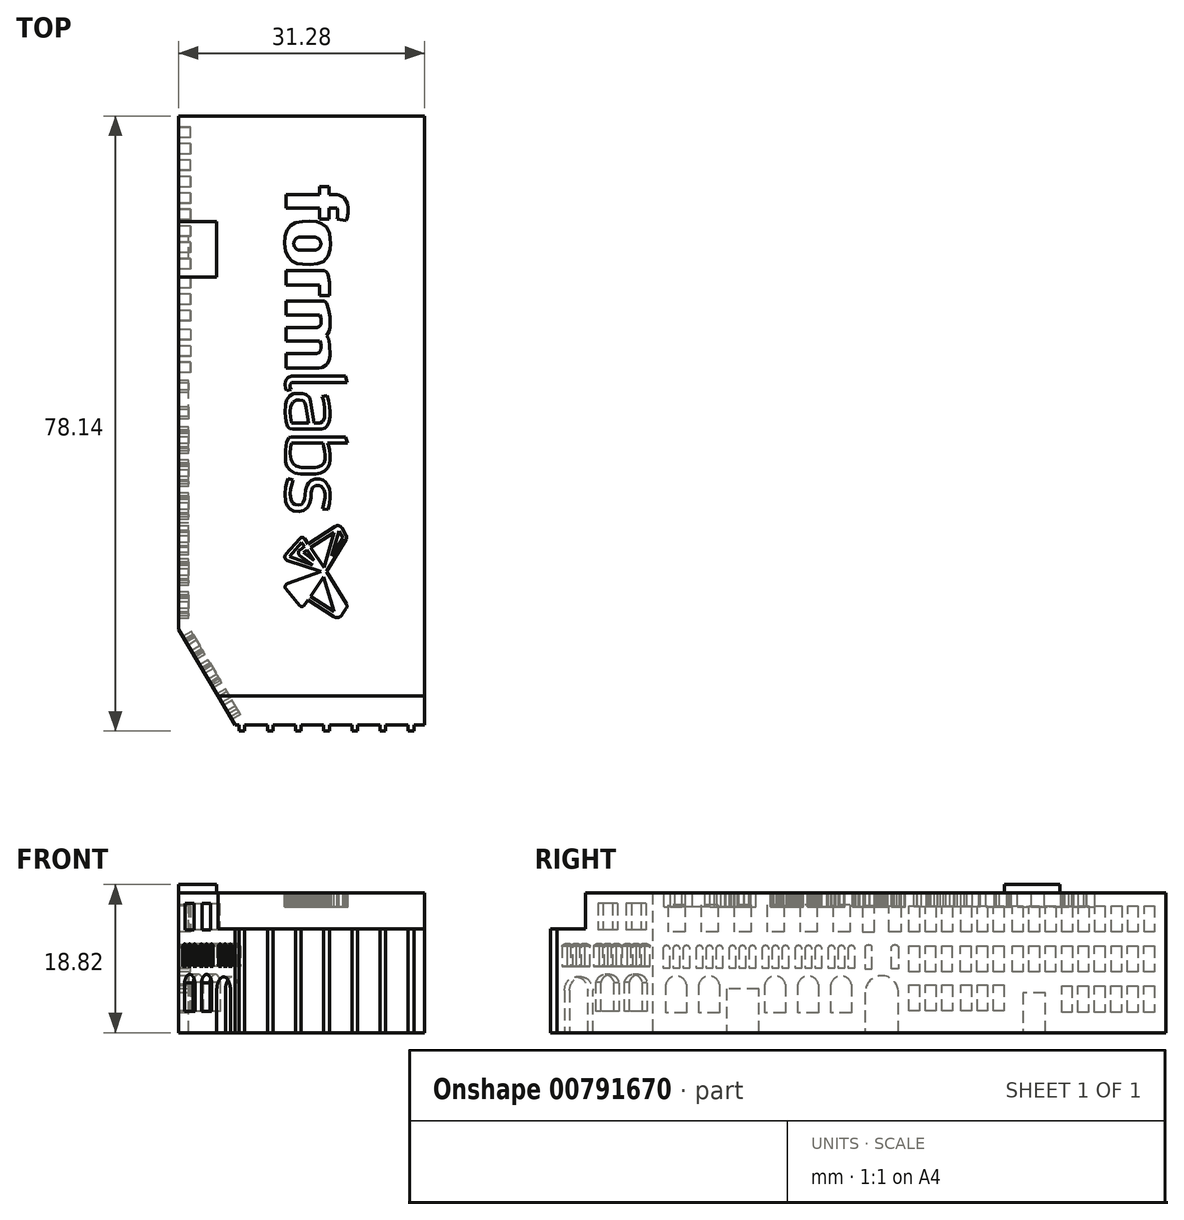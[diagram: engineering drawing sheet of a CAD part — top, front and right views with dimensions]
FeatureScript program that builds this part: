
annotation { "Feature Type Name" : "Feature", "Feature Type Description" : "" }
export const myFeature = defineFeature(function(context is Context, id is Id, definition is map)
    precondition{}
    {
        {
            var Q0;
            Q0=qCreatedBy(makeId("Top.planeOp"),FACE);
            var sketch = newSketch(context, id + "F0", { "sketchPlane" : qUnion([Q0])});
            skLineSegment(sketch, "E0", {"start": v(-16.51, -36.2) * mm, "end": v(-16.51, 29.03) * mm});
            skLineSegment(sketch, "E1", {"start": v(-16.51, 29.03) * mm, "end": v(14.77, 29.03) * mm});
            skLineSegment(sketch, "E2", {"start": v(14.77, 29.03) * mm, "end": v(14.77, -48.33) * mm});
            skLineSegment(sketch, "E3", {"start": v(14.77, -48.33) * mm, "end": v(-9.3, -48.33) * mm});
            skLineSegment(sketch, "E4", {"start": v(-9.3, -48.33) * mm, "end": v(-16.51, -36.2) * mm});
            skSolve(sketch);
        }
        {
            var Q0;
            Q0 = qSketchRegion(id + "F0", true);
            extrude(context, id + "F1", {"entities" : qUnion([Q0]), "depth" : 13.2 * mm, "offsetDistance" : 25.4 * mm});
        }
        {
            var Q0;
            Q0=makeQuery(id+"F1.opExtrude","CAP_FACE",FACE,{"disambiguationData":[OSD([sQuery(id+"F0.wireOp",EDGE,"E0"),sQuery(id+"F0.wireOp",EDGE,"E1"),sQuery(id+"F0.wireOp",EDGE,"E2"),sQuery(id+"F0.wireOp",EDGE,"E3"),sQuery(id+"F0.wireOp",EDGE,"E4")])],"isStart":false});
            var sketch = newSketch(context, id + "F2", { "sketchPlane" : qUnion([Q0])});
            skLineSegment(sketch, "E5", {"start": v(14.77, -44.68) * mm, "end": v(-11.47, -44.68) * mm});
            skLineSegment(sketch, "E6", {"start": v(-11.47, -44.68) * mm, "end": v(-16.51, -36.2) * mm});
            skLineSegment(sketch, "E7", {"start": v(-16.51, -36.2) * mm, "end": v(-16.51, 29.03) * mm});
            skLineSegment(sketch, "E8", {"start": v(-16.51, 29.03) * mm, "end": v(14.77, 29.03) * mm});
            skLineSegment(sketch, "E9", {"start": v(14.77, 29.03) * mm, "end": v(14.77, -44.68) * mm});
            skSolve(sketch);
        }
        {
            var Q0;
            Q0 = qSketchRegion(id + "F2", true);
            extrude(context, id + "F3", {"entities" : qUnion([Q0]), "operationType" : NewBodyOperationType.ADD, "depth" : 4.57 * mm, "offsetDistance" : 25.4 * mm});
        }
        {
            var Q0;
            Q0=makeQuery(id+"F3.opExtrude","CAP_FACE",FACE,{"disambiguationData":[OSD([sQuery(id+"F2.wireOp",EDGE,"E5"),sQuery(id+"F2.wireOp",EDGE,"E6"),sQuery(id+"F2.wireOp",EDGE,"E7"),sQuery(id+"F2.wireOp",EDGE,"E8"),sQuery(id+"F2.wireOp",EDGE,"E9")])],"isStart":false});
            var sketch = newSketch(context, id + "F4", { "sketchPlane" : qUnion([Q0])});
            skLineSegment(sketch, "E10", {"start": v(-16.51, 15.61) * mm, "end": v(-11.69, 15.61) * mm});
            skLineSegment(sketch, "E11", {"start": v(-11.69, 15.61) * mm, "end": v(-11.69, 8.53) * mm});
            skLineSegment(sketch, "E12", {"start": v(-11.69, 8.53) * mm, "end": v(-16.51, 8.53) * mm});
            skLineSegment(sketch, "E13", {"start": v(-16.51, 8.53) * mm, "end": v(-16.51, 15.61) * mm});
            skSolve(sketch);
        }
        {
            var Q0;
            Q0 = qSketchRegion(id + "F4", true);
            extrude(context, id + "F5", {"entities" : qUnion([Q0]), "operationType" : NewBodyOperationType.ADD, "depth" : 1.04 * mm, "offsetDistance" : 25.4 * mm});
        }
        {
            var Q0;
            Q0=makeQuery(id+"F5.boolean.opBoolean","MERGE",FACE,{"derivedFrom":[makeQuery(id+"F3.boolean.opBoolean","MERGE",FACE,{"derivedFrom":[makeQuery(id+"F1.opExtrude","SWEPT_FACE",FACE,{"disambiguationData":[OSD([sQuery(id+"F0.wireOp",EDGE,"E0")])]}),makeQuery(id+"F3.opExtrude","SWEPT_FACE",FACE,{"disambiguationData":[OSD([sQuery(id+"F2.wireOp",EDGE,"E7")])]})]}),makeQuery(id+"F5.opExtrude","SWEPT_FACE",FACE,{"disambiguationData":[OSD([sQuery(id+"F4.wireOp",EDGE,"E13")])]})]});
            var sketch = newSketch(context, id + "F6", { "sketchPlane" : qUnion([Q0])});
            skLineSegment(sketch, "E14", {"start": v(-27.6, 16.12) * mm, "end": v(-27.6, 12.8) * mm});
            skLineSegment(sketch, "E15", {"start": v(-27.6, 12.8) * mm, "end": v(-26.29, 12.8) * mm});
            skLineSegment(sketch, "E16", {"start": v(-26.29, 12.8) * mm, "end": v(-26.29, 16.12) * mm});
            skLineSegment(sketch, "E17", {"start": v(-26.29, 16.12) * mm, "end": v(-27.6, 16.12) * mm});
            skLineSegment(sketch, "E18.1.0.0", {"start": v(-25.52, 16.12) * mm, "end": v(-25.52, 12.8) * mm});
            skLineSegment(sketch, "E18.1.0.1", {"start": v(-25.52, 12.8) * mm, "end": v(-24.2, 12.8) * mm});
            skLineSegment(sketch, "E18.1.0.2", {"start": v(-24.2, 12.8) * mm, "end": v(-24.2, 16.12) * mm});
            skLineSegment(sketch, "E18.1.0.3", {"start": v(-24.2, 16.12) * mm, "end": v(-25.52, 16.12) * mm});
            skLineSegment(sketch, "E18.2.0.0", {"start": v(-23.44, 16.12) * mm, "end": v(-23.44, 12.8) * mm});
            skLineSegment(sketch, "E18.2.0.1", {"start": v(-23.44, 12.8) * mm, "end": v(-22.12, 12.8) * mm});
            skLineSegment(sketch, "E18.2.0.2", {"start": v(-22.12, 12.8) * mm, "end": v(-22.12, 16.12) * mm});
            skLineSegment(sketch, "E18.2.0.3", {"start": v(-22.12, 16.12) * mm, "end": v(-23.44, 16.12) * mm});
            skLineSegment(sketch, "E18.direction1", {"start": v(-27.6, 12.8) * mm, "end": v(-25.52, 12.8) * mm, "construction": true});
            skLineSegment(sketch, "E19.1.0.0", {"start": v(-24.19, 7.7) * mm, "end": v(-24.19, 11.02) * mm});
            skLineSegment(sketch, "E19.1.0.1", {"start": v(-24.19, 11.02) * mm, "end": v(-25.5, 11.02) * mm});
            skLineSegment(sketch, "E19.1.0.2", {"start": v(-27.58, 7.7) * mm, "end": v(-25.5, 7.7) * mm, "construction": true});
            skLineSegment(sketch, "E19.1.0.3", {"start": v(-22.1, 11.02) * mm, "end": v(-23.42, 11.02) * mm});
            skLineSegment(sketch, "E19.1.0.4", {"start": v(-25.5, 7.7) * mm, "end": v(-24.19, 7.7) * mm});
            skLineSegment(sketch, "E19.1.0.5", {"start": v(-23.42, 11.02) * mm, "end": v(-23.42, 7.7) * mm});
            skLineSegment(sketch, "E19.1.0.6", {"start": v(-22.1, 7.7) * mm, "end": v(-22.1, 11.02) * mm});
            skLineSegment(sketch, "E19.1.0.7", {"start": v(-25.5, 11.02) * mm, "end": v(-25.5, 7.7) * mm});
            skLineSegment(sketch, "E19.1.0.8", {"start": v(-23.42, 7.7) * mm, "end": v(-22.1, 7.7) * mm});
            skLineSegment(sketch, "E19.1.0.9", {"start": v(-26.27, 11.02) * mm, "end": v(-27.58, 11.02) * mm});
            skLineSegment(sketch, "E19.1.0.10", {"start": v(-27.58, 11.02) * mm, "end": v(-27.58, 7.7) * mm});
            skLineSegment(sketch, "E19.1.0.11", {"start": v(-26.27, 7.7) * mm, "end": v(-26.27, 11.02) * mm});
            skLineSegment(sketch, "E19.1.0.12", {"start": v(-27.58, 7.7) * mm, "end": v(-26.27, 7.7) * mm});
            skLineSegment(sketch, "E19.2.0.0", {"start": v(-24.17, 2.6) * mm, "end": v(-24.17, 5.92) * mm});
            skLineSegment(sketch, "E19.2.0.1", {"start": v(-24.17, 5.92) * mm, "end": v(-25.48, 5.92) * mm});
            skLineSegment(sketch, "E19.2.0.2", {"start": v(-27.57, 2.6) * mm, "end": v(-25.48, 2.6) * mm, "construction": true});
            skLineSegment(sketch, "E19.2.0.3", {"start": v(-22.08, 5.92) * mm, "end": v(-23.4, 5.92) * mm});
            skLineSegment(sketch, "E19.2.0.4", {"start": v(-25.48, 2.6) * mm, "end": v(-24.17, 2.6) * mm});
            skLineSegment(sketch, "E19.2.0.5", {"start": v(-23.4, 5.92) * mm, "end": v(-23.4, 2.6) * mm});
            skLineSegment(sketch, "E19.2.0.6", {"start": v(-22.08, 2.6) * mm, "end": v(-22.08, 5.92) * mm});
            skLineSegment(sketch, "E19.2.0.7", {"start": v(-25.48, 5.92) * mm, "end": v(-25.48, 2.6) * mm});
            skLineSegment(sketch, "E19.2.0.8", {"start": v(-23.4, 2.6) * mm, "end": v(-22.08, 2.6) * mm});
            skLineSegment(sketch, "E19.2.0.9", {"start": v(-26.25, 5.92) * mm, "end": v(-27.57, 5.92) * mm});
            skLineSegment(sketch, "E19.2.0.10", {"start": v(-27.57, 5.92) * mm, "end": v(-27.57, 2.6) * mm});
            skLineSegment(sketch, "E19.2.0.11", {"start": v(-26.25, 2.6) * mm, "end": v(-26.25, 5.92) * mm});
            skLineSegment(sketch, "E19.2.0.12", {"start": v(-27.57, 2.6) * mm, "end": v(-26.25, 2.6) * mm});
            skLineSegment(sketch, "E19.direction1", {"start": v(-27.6, 12.8) * mm, "end": v(-27.58, 7.7) * mm, "construction": true});
            skLineSegment(sketch, "E20.1.0.0", {"start": v(-20.01, 12.8) * mm, "end": v(-20.01, 16.12) * mm});
            skLineSegment(sketch, "E20.1.0.1", {"start": v(-20.01, 16.12) * mm, "end": v(-21.33, 16.12) * mm});
            skLineSegment(sketch, "E20.1.0.2", {"start": v(-17.13, 2.6) * mm, "end": v(-15.81, 2.6) * mm});
            skLineSegment(sketch, "E20.1.0.3", {"start": v(-15.85, 12.8) * mm, "end": v(-15.85, 16.12) * mm});
            skLineSegment(sketch, "E20.1.0.4", {"start": v(-17.13, 5.92) * mm, "end": v(-17.13, 2.6) * mm});
            skLineSegment(sketch, "E20.1.0.5", {"start": v(-21.31, 7.7) * mm, "end": v(-19.23, 7.7) * mm, "construction": true});
            skLineSegment(sketch, "E20.1.0.6", {"start": v(-20, 11.02) * mm, "end": v(-21.31, 11.02) * mm});
            skLineSegment(sketch, "E20.1.0.7", {"start": v(-19.25, 16.12) * mm, "end": v(-19.25, 12.8) * mm});
            skLineSegment(sketch, "E20.1.0.8", {"start": v(-21.33, 16.12) * mm, "end": v(-21.33, 12.8) * mm});
            skLineSegment(sketch, "E20.1.0.9", {"start": v(-17.91, 7.7) * mm, "end": v(-17.91, 11.02) * mm});
            skLineSegment(sketch, "E20.1.0.10", {"start": v(-19.25, 12.8) * mm, "end": v(-17.93, 12.8) * mm});
            skLineSegment(sketch, "E20.1.0.11", {"start": v(-17.91, 11.02) * mm, "end": v(-19.23, 11.02) * mm});
            skLineSegment(sketch, "E20.1.0.12", {"start": v(-17.93, 12.8) * mm, "end": v(-17.93, 16.12) * mm});
            skLineSegment(sketch, "E20.1.0.13", {"start": v(-17.93, 16.12) * mm, "end": v(-19.25, 16.12) * mm});
            skLineSegment(sketch, "E20.1.0.14", {"start": v(-17.16, 12.8) * mm, "end": v(-15.85, 12.8) * mm});
            skLineSegment(sketch, "E20.1.0.15", {"start": v(-17.16, 16.12) * mm, "end": v(-17.16, 12.8) * mm});
            skLineSegment(sketch, "E20.1.0.16", {"start": v(-17.14, 11.02) * mm, "end": v(-17.14, 7.7) * mm});
            skLineSegment(sketch, "E20.1.0.17", {"start": v(-15.85, 16.12) * mm, "end": v(-17.16, 16.12) * mm});
            skLineSegment(sketch, "E20.1.0.18", {"start": v(-21.33, 12.8) * mm, "end": v(-19.25, 12.8) * mm, "construction": true});
            skLineSegment(sketch, "E20.1.0.19", {"start": v(-17.9, 2.6) * mm, "end": v(-17.9, 5.92) * mm});
            skLineSegment(sketch, "E20.1.0.20", {"start": v(-19.98, 5.92) * mm, "end": v(-21.3, 5.92) * mm});
            skLineSegment(sketch, "E20.1.0.21", {"start": v(-15.83, 7.7) * mm, "end": v(-15.83, 11.02) * mm});
            skLineSegment(sketch, "E20.1.0.22", {"start": v(-15.81, 2.6) * mm, "end": v(-15.81, 5.92) * mm});
            skLineSegment(sketch, "E20.1.0.23", {"start": v(-15.83, 11.02) * mm, "end": v(-17.14, 11.02) * mm});
            skLineSegment(sketch, "E20.1.0.24", {"start": v(-17.9, 5.92) * mm, "end": v(-19.2, 5.92) * mm});
            skLineSegment(sketch, "E20.1.0.25", {"start": v(-15.81, 5.92) * mm, "end": v(-17.13, 5.92) * mm});
            skLineSegment(sketch, "E20.1.0.26", {"start": v(-21.3, 5.92) * mm, "end": v(-21.3, 2.6) * mm});
            skLineSegment(sketch, "E20.1.0.27", {"start": v(-19.23, 11.02) * mm, "end": v(-19.23, 7.7) * mm});
            skLineSegment(sketch, "E20.1.0.28", {"start": v(-21.33, 12.8) * mm, "end": v(-21.31, 7.7) * mm, "construction": true});
            skLineSegment(sketch, "E20.1.0.29", {"start": v(-19.2, 5.92) * mm, "end": v(-19.2, 2.6) * mm});
            skLineSegment(sketch, "E20.1.0.30", {"start": v(-19.23, 7.7) * mm, "end": v(-17.91, 7.7) * mm});
            skLineSegment(sketch, "E20.1.0.31", {"start": v(-21.3, 2.6) * mm, "end": v(-19.2, 2.6) * mm, "construction": true});
            skLineSegment(sketch, "E20.1.0.32", {"start": v(-19.98, 2.6) * mm, "end": v(-19.98, 5.92) * mm});
            skLineSegment(sketch, "E20.1.0.33", {"start": v(-19.2, 2.6) * mm, "end": v(-17.9, 2.6) * mm});
            skLineSegment(sketch, "E20.1.0.34", {"start": v(-17.14, 7.7) * mm, "end": v(-15.83, 7.7) * mm});
            skLineSegment(sketch, "E20.1.0.35", {"start": v(-20, 7.7) * mm, "end": v(-20, 11.02) * mm});
            skLineSegment(sketch, "E20.1.0.36", {"start": v(-21.3, 2.6) * mm, "end": v(-19.98, 2.6) * mm});
            skLineSegment(sketch, "E20.1.0.37", {"start": v(-21.33, 12.8) * mm, "end": v(-20.01, 12.8) * mm});
            skLineSegment(sketch, "E20.1.0.38", {"start": v(-21.31, 7.7) * mm, "end": v(-20, 7.7) * mm});
            skLineSegment(sketch, "E20.1.0.39", {"start": v(-21.31, 11.02) * mm, "end": v(-21.31, 7.7) * mm});
            skLineSegment(sketch, "E20.2.0.0", {"start": v(-13.74, 12.8) * mm, "end": v(-13.74, 16.12) * mm});
            skLineSegment(sketch, "E20.2.0.1", {"start": v(-13.74, 16.12) * mm, "end": v(-15.05, 16.12) * mm});
            skLineSegment(sketch, "E20.2.0.3", {"start": v(-9.57, 12.8) * mm, "end": v(-9.57, 16.12) * mm});
            skLineSegment(sketch, "E20.2.0.5", {"start": v(-15.04, 7.7) * mm, "end": v(-12.95, 7.7) * mm, "construction": true});
            skLineSegment(sketch, "E20.2.0.6", {"start": v(-13.72, 11.02) * mm, "end": v(-15.04, 11.02) * mm});
            skLineSegment(sketch, "E20.2.0.7", {"start": v(-12.97, 16.12) * mm, "end": v(-12.97, 12.8) * mm});
            skLineSegment(sketch, "E20.2.0.8", {"start": v(-15.05, 16.12) * mm, "end": v(-15.05, 12.8) * mm});
            skLineSegment(sketch, "E20.2.0.9", {"start": v(-11.64, 7.7) * mm, "end": v(-11.64, 11.02) * mm});
            skLineSegment(sketch, "E20.2.0.10", {"start": v(-12.97, 12.8) * mm, "end": v(-11.66, 12.8) * mm});
            skLineSegment(sketch, "E20.2.0.11", {"start": v(-11.64, 11.02) * mm, "end": v(-12.95, 11.02) * mm});
            skLineSegment(sketch, "E20.2.0.12", {"start": v(-11.66, 12.8) * mm, "end": v(-11.66, 16.12) * mm});
            skLineSegment(sketch, "E20.2.0.13", {"start": v(-11.66, 16.12) * mm, "end": v(-12.97, 16.12) * mm});
            skLineSegment(sketch, "E20.2.0.14", {"start": v(-10.89, 12.8) * mm, "end": v(-9.57, 12.8) * mm});
            skLineSegment(sketch, "E20.2.0.15", {"start": v(-10.89, 16.12) * mm, "end": v(-10.89, 12.8) * mm});
            skLineSegment(sketch, "E20.2.0.16", {"start": v(-10.87, 11.02) * mm, "end": v(-10.87, 7.7) * mm});
            skLineSegment(sketch, "E20.2.0.17", {"start": v(-9.57, 16.12) * mm, "end": v(-10.89, 16.12) * mm});
            skLineSegment(sketch, "E20.2.0.18", {"start": v(-15.05, 12.8) * mm, "end": v(-12.97, 12.8) * mm, "construction": true});
            skLineSegment(sketch, "E20.2.0.21", {"start": v(-9.55, 7.7) * mm, "end": v(-9.55, 11.02) * mm});
            skLineSegment(sketch, "E20.2.0.23", {"start": v(-9.55, 11.02) * mm, "end": v(-10.87, 11.02) * mm});
            skLineSegment(sketch, "E20.2.0.27", {"start": v(-12.95, 11.02) * mm, "end": v(-12.95, 7.7) * mm});
            skLineSegment(sketch, "E20.2.0.28", {"start": v(-15.05, 12.8) * mm, "end": v(-15.04, 7.7) * mm, "construction": true});
            skLineSegment(sketch, "E20.2.0.30", {"start": v(-12.95, 7.7) * mm, "end": v(-11.64, 7.7) * mm});
            skLineSegment(sketch, "E20.2.0.34", {"start": v(-10.87, 7.7) * mm, "end": v(-9.55, 7.7) * mm});
            skLineSegment(sketch, "E20.2.0.35", {"start": v(-13.72, 7.7) * mm, "end": v(-13.72, 11.02) * mm});
            skLineSegment(sketch, "E20.2.0.37", {"start": v(-15.05, 12.8) * mm, "end": v(-13.74, 12.8) * mm});
            skLineSegment(sketch, "E20.2.0.38", {"start": v(-15.04, 7.7) * mm, "end": v(-13.72, 7.7) * mm});
            skLineSegment(sketch, "E20.2.0.39", {"start": v(-15.04, 11.02) * mm, "end": v(-15.04, 7.7) * mm});
            skLineSegment(sketch, "E20.direction1", {"start": v(-27.57, 2.6) * mm, "end": v(-21.3, 2.6) * mm, "construction": true});
            skLineSegment(sketch, "E21.1.0.0", {"start": v(-8.48, 12.8) * mm, "end": v(-6.4, 12.8) * mm, "construction": true});
            skLineSegment(sketch, "E21.1.0.1", {"start": v(-5.06, 7.7) * mm, "end": v(-5.06, 11.02) * mm});
            skLineSegment(sketch, "E21.1.0.2", {"start": v(-7.14, 7.7) * mm, "end": v(-7.14, 11.02) * mm});
            skLineSegment(sketch, "E21.1.0.3", {"start": v(-7.16, 12.8) * mm, "end": v(-7.16, 16.12) * mm});
            skLineSegment(sketch, "E21.1.0.4", {"start": v(-7.16, 16.12) * mm, "end": v(-8.48, 16.12) * mm});
            skLineSegment(sketch, "E21.1.0.5", {"start": v(-2.98, 7.7) * mm, "end": v(-2.98, 11.02) * mm});
            skLineSegment(sketch, "E21.1.0.6", {"start": v(-6.4, 12.8) * mm, "end": v(-5.08, 12.8) * mm});
            skLineSegment(sketch, "E21.1.0.7", {"start": v(-8.48, 16.12) * mm, "end": v(-8.48, 12.8) * mm});
            skLineSegment(sketch, "E21.1.0.8", {"start": v(-3, 16.12) * mm, "end": v(-4.31, 16.12) * mm});
            skLineSegment(sketch, "E21.1.0.9", {"start": v(-4.3, 7.7) * mm, "end": v(-2.98, 7.7) * mm});
            skLineSegment(sketch, "E21.1.0.10", {"start": v(-6.4, 16.12) * mm, "end": v(-6.4, 12.8) * mm});
            skLineSegment(sketch, "E21.1.0.11", {"start": v(-6.38, 7.7) * mm, "end": v(-5.06, 7.7) * mm});
            skLineSegment(sketch, "E21.1.0.12", {"start": v(-4.3, 11.02) * mm, "end": v(-4.3, 7.7) * mm});
            skLineSegment(sketch, "E21.1.0.13", {"start": v(-4.31, 12.8) * mm, "end": v(-3, 12.8) * mm});
            skLineSegment(sketch, "E21.1.0.14", {"start": v(-7.14, 11.02) * mm, "end": v(-8.46, 11.02) * mm});
            skLineSegment(sketch, "E21.1.0.15", {"start": v(-4.31, 16.12) * mm, "end": v(-4.31, 12.8) * mm});
            skLineSegment(sketch, "E21.1.0.16", {"start": v(-8.48, 12.8) * mm, "end": v(-8.46, 7.7) * mm, "construction": true});
            skLineSegment(sketch, "E21.1.0.17", {"start": v(-5.08, 16.12) * mm, "end": v(-6.4, 16.12) * mm});
            skLineSegment(sketch, "E21.1.0.18", {"start": v(-5.08, 12.8) * mm, "end": v(-5.08, 16.12) * mm});
            skLineSegment(sketch, "E21.1.0.19", {"start": v(-3, 12.8) * mm, "end": v(-3, 16.12) * mm});
            skLineSegment(sketch, "E21.1.0.20", {"start": v(-2.98, 11.02) * mm, "end": v(-4.3, 11.02) * mm});
            skLineSegment(sketch, "E21.1.0.21", {"start": v(-8.46, 7.7) * mm, "end": v(-6.38, 7.7) * mm, "construction": true});
            skLineSegment(sketch, "E21.1.0.22", {"start": v(-6.38, 11.02) * mm, "end": v(-6.38, 7.7) * mm});
            skLineSegment(sketch, "E21.1.0.23", {"start": v(-5.06, 11.02) * mm, "end": v(-6.38, 11.02) * mm});
            skLineSegment(sketch, "E21.1.0.24", {"start": v(-8.48, 12.8) * mm, "end": v(-7.16, 12.8) * mm});
            skLineSegment(sketch, "E21.1.0.25", {"start": v(-8.46, 11.02) * mm, "end": v(-8.46, 7.7) * mm});
            skLineSegment(sketch, "E21.1.0.26", {"start": v(-8.46, 7.7) * mm, "end": v(-7.14, 7.7) * mm});
            skLineSegment(sketch, "E21.2.0.0", {"start": v(-1.9, 12.8) * mm, "end": v(0.19, 12.8) * mm, "construction": true});
            skLineSegment(sketch, "E21.2.0.1", {"start": v(1.52, 7.7) * mm, "end": v(1.52, 11.02) * mm});
            skLineSegment(sketch, "E21.2.0.2", {"start": v(-0.56, 7.7) * mm, "end": v(-0.56, 11.02) * mm});
            skLineSegment(sketch, "E21.2.0.3", {"start": v(-0.58, 12.8) * mm, "end": v(-0.58, 16.12) * mm});
            skLineSegment(sketch, "E21.2.0.4", {"start": v(-0.58, 16.12) * mm, "end": v(-1.9, 16.12) * mm});
            skLineSegment(sketch, "E21.2.0.5", {"start": v(3.6, 7.7) * mm, "end": v(3.6, 11.02) * mm});
            skLineSegment(sketch, "E21.2.0.6", {"start": v(0.19, 12.8) * mm, "end": v(1.5, 12.8) * mm});
            skLineSegment(sketch, "E21.2.0.7", {"start": v(-1.9, 16.12) * mm, "end": v(-1.9, 12.8) * mm});
            skLineSegment(sketch, "E21.2.0.8", {"start": v(3.58, 16.12) * mm, "end": v(2.27, 16.12) * mm});
            skLineSegment(sketch, "E21.2.0.9", {"start": v(2.29, 7.7) * mm, "end": v(3.6, 7.7) * mm});
            skLineSegment(sketch, "E21.2.0.10", {"start": v(0.19, 16.12) * mm, "end": v(0.19, 12.8) * mm});
            skLineSegment(sketch, "E21.2.0.11", {"start": v(0.2, 7.7) * mm, "end": v(1.52, 7.7) * mm});
            skLineSegment(sketch, "E21.2.0.12", {"start": v(2.29, 11.02) * mm, "end": v(2.29, 7.7) * mm});
            skLineSegment(sketch, "E21.2.0.13", {"start": v(2.27, 12.8) * mm, "end": v(3.58, 12.8) * mm});
            skLineSegment(sketch, "E21.2.0.14", {"start": v(-0.56, 11.02) * mm, "end": v(-1.88, 11.02) * mm});
            skLineSegment(sketch, "E21.2.0.15", {"start": v(2.27, 16.12) * mm, "end": v(2.27, 12.8) * mm});
            skLineSegment(sketch, "E21.2.0.16", {"start": v(-1.9, 12.8) * mm, "end": v(-1.88, 7.7) * mm, "construction": true});
            skLineSegment(sketch, "E21.2.0.17", {"start": v(1.5, 16.12) * mm, "end": v(0.19, 16.12) * mm});
            skLineSegment(sketch, "E21.2.0.18", {"start": v(1.5, 12.8) * mm, "end": v(1.5, 16.12) * mm});
            skLineSegment(sketch, "E21.2.0.19", {"start": v(3.58, 12.8) * mm, "end": v(3.58, 16.12) * mm});
            skLineSegment(sketch, "E21.2.0.20", {"start": v(3.6, 11.02) * mm, "end": v(2.29, 11.02) * mm});
            skLineSegment(sketch, "E21.2.0.21", {"start": v(-1.88, 7.7) * mm, "end": v(0.2, 7.7) * mm, "construction": true});
            skLineSegment(sketch, "E21.2.0.22", {"start": v(0.2, 11.02) * mm, "end": v(0.2, 7.7) * mm});
            skLineSegment(sketch, "E21.2.0.23", {"start": v(1.52, 11.02) * mm, "end": v(0.2, 11.02) * mm});
            skLineSegment(sketch, "E21.2.0.24", {"start": v(-1.9, 12.8) * mm, "end": v(-0.58, 12.8) * mm});
            skLineSegment(sketch, "E21.2.0.25", {"start": v(-1.88, 11.02) * mm, "end": v(-1.88, 7.7) * mm});
            skLineSegment(sketch, "E21.2.0.26", {"start": v(-1.88, 7.7) * mm, "end": v(-0.56, 7.7) * mm});
            skLineSegment(sketch, "E21.direction1", {"start": v(-15.04, 7.7) * mm, "end": v(-8.46, 7.7) * mm, "construction": true});
            skLineSegment(sketch, "E22.1.0.0", {"start": v(-7.17, 6.07) * mm, "end": v(-8.48, 6.07) * mm});
            skLineSegment(sketch, "E22.1.0.1", {"start": v(0.18, 6.07) * mm, "end": v(0.18, 2.74) * mm});
            skLineSegment(sketch, "E22.1.0.2", {"start": v(-5.08, 2.74) * mm, "end": v(-5.08, 6.07) * mm});
            skLineSegment(sketch, "E22.1.0.3", {"start": v(3.58, 6.07) * mm, "end": v(2.26, 6.07) * mm});
            skLineSegment(sketch, "E22.1.0.4", {"start": v(-0.59, 2.74) * mm, "end": v(-0.59, 6.07) * mm});
            skLineSegment(sketch, "E22.1.0.5", {"start": v(-4.32, 6.07) * mm, "end": v(-4.32, 2.74) * mm});
            skLineSegment(sketch, "E22.1.0.6", {"start": v(1.5, 2.74) * mm, "end": v(1.5, 6.07) * mm});
            skLineSegment(sketch, "E22.1.0.7", {"start": v(-6.4, 6.07) * mm, "end": v(-6.4, 2.74) * mm});
            skLineSegment(sketch, "E22.1.0.8", {"start": v(-5.08, 6.07) * mm, "end": v(-6.4, 6.07) * mm});
            skLineSegment(sketch, "E22.1.0.9", {"start": v(2.26, 6.07) * mm, "end": v(2.26, 2.74) * mm});
            skLineSegment(sketch, "E22.1.0.10", {"start": v(0.18, 2.74) * mm, "end": v(1.5, 2.74) * mm});
            skLineSegment(sketch, "E22.1.0.11", {"start": v(-6.4, 2.74) * mm, "end": v(-5.08, 2.74) * mm});
            skLineSegment(sketch, "E22.1.0.12", {"start": v(-4.32, 2.74) * mm, "end": v(-3, 2.74) * mm});
            skLineSegment(sketch, "E22.1.0.13", {"start": v(-8.48, 6.07) * mm, "end": v(-8.48, 2.74) * mm});
            skLineSegment(sketch, "E22.1.0.14", {"start": v(-0.59, 6.07) * mm, "end": v(-1.9, 6.07) * mm});
            skLineSegment(sketch, "E22.1.0.15", {"start": v(3.58, 2.74) * mm, "end": v(3.58, 6.07) * mm});
            skLineSegment(sketch, "E22.1.0.16", {"start": v(-1.9, 2.74) * mm, "end": v(0.18, 2.74) * mm, "construction": true});
            skLineSegment(sketch, "E22.1.0.17", {"start": v(1.5, 6.07) * mm, "end": v(0.18, 6.07) * mm});
            skLineSegment(sketch, "E22.1.0.18", {"start": v(-7.17, 2.74) * mm, "end": v(-7.17, 6.07) * mm});
            skLineSegment(sketch, "E22.1.0.19", {"start": v(-1.9, 6.07) * mm, "end": v(-1.9, 2.74) * mm});
            skLineSegment(sketch, "E22.1.0.20", {"start": v(2.26, 2.74) * mm, "end": v(3.58, 2.74) * mm});
            skLineSegment(sketch, "E22.1.0.21", {"start": v(-3, 6.07) * mm, "end": v(-4.32, 6.07) * mm});
            skLineSegment(sketch, "E22.1.0.22", {"start": v(-8.48, 2.74) * mm, "end": v(-6.4, 2.74) * mm, "construction": true});
            skLineSegment(sketch, "E22.1.0.23", {"start": v(-3, 2.74) * mm, "end": v(-3, 6.07) * mm});
            skLineSegment(sketch, "E22.1.0.24", {"start": v(-8.48, 2.74) * mm, "end": v(-7.17, 2.74) * mm});
            skLineSegment(sketch, "E22.1.0.25", {"start": v(-1.9, 2.74) * mm, "end": v(-0.59, 2.74) * mm});
            skLineSegment(sketch, "E22.direction1", {"start": v(-8.46, 7.7) * mm, "end": v(-8.48, 2.74) * mm, "construction": true});
            skSolve(sketch);
        }
        {
            var Q0;
            Q0 = qSketchRegion(id + "F6", true);
            extrude(context, id + "F7", {"entities" : qUnion([Q0]), "operationType" : NewBodyOperationType.REMOVE, "oppositeDirection" : true, "depth" : 1.52 * mm, "offsetDistance" : 25.4 * mm});
        }
        {
            var Q0;
            Q0=makeQuery(id+"F5.boolean.opBoolean","MERGE",FACE,{"derivedFrom":[makeQuery(id+"F3.boolean.opBoolean","MERGE",FACE,{"derivedFrom":[makeQuery(id+"F1.opExtrude","SWEPT_FACE",FACE,{"disambiguationData":[OSD([sQuery(id+"F0.wireOp",EDGE,"E0")])]}),makeQuery(id+"F3.opExtrude","SWEPT_FACE",FACE,{"disambiguationData":[OSD([sQuery(id+"F2.wireOp",EDGE,"E7")])]})]}),makeQuery(id+"F5.opExtrude","SWEPT_FACE",FACE,{"disambiguationData":[OSD([sQuery(id+"F4.wireOp",EDGE,"E13")])]})]});
            var sketch = newSketch(context, id + "F8", { "sketchPlane" : qUnion([Q0])});
            skLineSegment(sketch, "E23", {"start": v(-13.72, 0) * mm, "end": v(-13.72, 5.08) * mm});
            skLineSegment(sketch, "E24", {"start": v(-13.72, 5.08) * mm, "end": v(-10.88, 5.08) * mm});
            skLineSegment(sketch, "E25", {"start": v(-10.88, 5.08) * mm, "end": v(-10.88, 0) * mm});
            skLineSegment(sketch, "E26", {"start": v(-10.88, 0) * mm, "end": v(-13.72, 0) * mm});
            skLineSegment(sketch, "E27", {"start": v(4.93, 0) * mm, "end": v(4.93, 5.12) * mm});
            skArc(sketch, "E28", {"start": v(9.15, 5.12) * mm, "mid": v(7.04, 7.23) * mm, "end": v(4.93, 5.12) * mm});
            skLineSegment(sketch, "E29", {"start": v(9.15, 5.12) * mm, "end": v(9.15, 0) * mm});
            skLineSegment(sketch, "E30", {"start": v(9.15, 0) * mm, "end": v(4.93, 0) * mm});
            skLineSegment(sketch, "E31", {"start": v(4.93, 10.95) * mm, "end": v(4.93, 8.11) * mm});
            skLineSegment(sketch, "E32", {"start": v(4.93, 8.11) * mm, "end": v(5.82, 8.11) * mm});
            skLineSegment(sketch, "E33", {"start": v(5.82, 8.11) * mm, "end": v(5.82, 10.95) * mm});
            skArc(sketch, "E34", {"start": v(5.82, 10.95) * mm, "mid": v(5.37, 11.13) * mm, "end": v(4.93, 10.95) * mm});
            skLineSegment(sketch, "E35", {"start": v(7.04, 5.12) * mm, "end": v(7.04, 0) * mm, "construction": true});
            skLineSegment(sketch, "E36.MirrorCS", {"start": v(9.15, 10.95) * mm, "end": v(9.15, 8.11) * mm});
            skLineSegment(sketch, "E37.MirrorCS", {"start": v(8.27, 8.11) * mm, "end": v(8.27, 10.95) * mm});
            skLineSegment(sketch, "E38.MirrorCS", {"start": v(9.15, 8.11) * mm, "end": v(8.27, 8.11) * mm});
            skArc(sketch, "E39.MirrorCS", {"start": v(8.27, 10.95) * mm, "mid": v(8.71, 11.13) * mm, "end": v(9.15, 10.95) * mm});
            skLineSegment(sketch, "E40", {"start": v(4.6, 16.12) * mm, "end": v(4.6, 12.83) * mm});
            skLineSegment(sketch, "E41", {"start": v(4.6, 12.83) * mm, "end": v(6.1, 12.83) * mm});
            skLineSegment(sketch, "E42", {"start": v(6.1, 12.83) * mm, "end": v(6.1, 16.12) * mm});
            skLineSegment(sketch, "E43", {"start": v(6.1, 16.12) * mm, "end": v(4.6, 16.12) * mm});
            skLineSegment(sketch, "E44.MirrorCS", {"start": v(7.98, 16.12) * mm, "end": v(9.47, 16.12) * mm});
            skLineSegment(sketch, "E45.MirrorCS", {"start": v(7.98, 12.83) * mm, "end": v(7.98, 16.12) * mm});
            skLineSegment(sketch, "E46.MirrorCS", {"start": v(9.47, 12.83) * mm, "end": v(7.98, 12.83) * mm});
            skLineSegment(sketch, "E47.MirrorCS", {"start": v(9.47, 16.12) * mm, "end": v(9.47, 12.83) * mm});
            skSolve(sketch);
        }
        {
            var Q0;
            Q0 = qSketchRegion(id + "F8", true);
            var Q1;
            Q1 = qConstructionFilter(qBodyType(qCreatedBy(id + "F8" ,EDGE), BodyType.WIRE), ConstructionObject.NO);
            extrude(context, id + "F9", {"entities" : qUnion([Q0]), "bodyType" : ToolBodyType.SURFACE, "operationType" : NewBodyOperationType.REMOVE, "surfaceEntities" : qUnion([Q1]), "oppositeDirection" : true, "depth" : 2.31 * mm, "offsetDistance" : 25.4 * mm});
        }
        {
            var Q0;
            Q0 = qSketchRegion(id + "F8", true);
            extrude(context, id + "F10", {"entities" : qUnion([Q0]), "operationType" : NewBodyOperationType.REMOVE, "oppositeDirection" : true, "depth" : 1.27 * mm, "offsetDistance" : 25.4 * mm});
        }
        {
            var Q0;
            Q0=makeQuery(id+"F5.boolean.opBoolean","MERGE",FACE,{"derivedFrom":[makeQuery(id+"F3.boolean.opBoolean","MERGE",FACE,{"derivedFrom":[makeQuery(id+"F1.opExtrude","SWEPT_FACE",FACE,{"disambiguationData":[OSD([sQuery(id+"F0.wireOp",EDGE,"E0")])]}),makeQuery(id+"F3.opExtrude","SWEPT_FACE",FACE,{"disambiguationData":[OSD([sQuery(id+"F2.wireOp",EDGE,"E7")])]})]}),makeQuery(id+"F5.opExtrude","SWEPT_FACE",FACE,{"disambiguationData":[OSD([sQuery(id+"F4.wireOp",EDGE,"E13")])]})]});
            var sketch = newSketch(context, id + "F11", { "sketchPlane" : qUnion([Q0])});
            skLineSegment(sketch, "E48", {"start": v(10.48, 8.25) * mm, "end": v(10.48, 10.78) * mm});
            skArc(sketch, "E49", {"start": v(11.32, 10.78) * mm, "mid": v(10.9, 11.06) * mm, "end": v(10.48, 10.78) * mm});
            skLineSegment(sketch, "E50", {"start": v(11.32, 10.78) * mm, "end": v(11.32, 8.25) * mm});
            skLineSegment(sketch, "E51", {"start": v(11.32, 8.25) * mm, "end": v(10.48, 8.25) * mm});
            skPoint(sketch, "E52", {"position": v(10.9, 11.06) * mm});
            skPoint(sketch, "E53.1.0.0", {"position": v(12.17, 11.06) * mm});
            skLineSegment(sketch, "E53.1.0.1", {"start": v(12.59, 10.78) * mm, "end": v(12.59, 8.25) * mm});
            skLineSegment(sketch, "E53.1.0.2", {"start": v(11.75, 8.25) * mm, "end": v(11.75, 10.78) * mm});
            skLineSegment(sketch, "E53.1.0.3", {"start": v(12.59, 8.25) * mm, "end": v(11.75, 8.25) * mm});
            skArc(sketch, "E53.1.0.4", {"start": v(12.59, 10.78) * mm, "mid": v(12.17, 11.06) * mm, "end": v(11.75, 10.78) * mm});
            skPoint(sketch, "E53.2.0.0", {"position": v(13.44, 11.06) * mm});
            skLineSegment(sketch, "E53.2.0.1", {"start": v(13.86, 10.78) * mm, "end": v(13.86, 8.25) * mm});
            skLineSegment(sketch, "E53.2.0.2", {"start": v(13.02, 8.25) * mm, "end": v(13.02, 10.78) * mm});
            skLineSegment(sketch, "E53.2.0.3", {"start": v(13.86, 8.25) * mm, "end": v(13.02, 8.25) * mm});
            skArc(sketch, "E53.2.0.4", {"start": v(13.86, 10.78) * mm, "mid": v(13.44, 11.06) * mm, "end": v(13.02, 10.78) * mm});
            skLineSegment(sketch, "E53.direction1", {"start": v(10.48, 8.25) * mm, "end": v(11.75, 8.25) * mm, "construction": true});
            skLineSegment(sketch, "E54.bottom", {"start": v(11.09, 16.22) * mm, "end": v(13.25, 16.22) * mm});
            skLineSegment(sketch, "E54.top", {"start": v(11.09, 12.83) * mm, "end": v(13.25, 12.83) * mm});
            skLineSegment(sketch, "E54.left", {"start": v(11.09, 16.22) * mm, "end": v(11.09, 12.83) * mm});
            skLineSegment(sketch, "E54.right", {"start": v(13.25, 16.22) * mm, "end": v(13.25, 12.83) * mm});
            skLineSegment(sketch, "E55", {"start": v(12.17, 16.22) * mm, "end": v(12.17, 12.83) * mm, "construction": true});
            skLineSegment(sketch, "E56.MirrorCS", {"start": v(11.31, 8.25) * mm, "end": v(11.31, 10.78) * mm});
            skLineSegment(sketch, "E57.MirrorCS", {"start": v(13.02, 10.78) * mm, "end": v(13.02, 8.25) * mm});
            skLineSegment(sketch, "E58", {"start": v(10.9, 6.14) * mm, "end": v(10.9, 2.5) * mm});
            skLineSegment(sketch, "E59", {"start": v(10.9, 2.5) * mm, "end": v(13.52, 2.5) * mm});
            skLineSegment(sketch, "E60", {"start": v(13.52, 2.5) * mm, "end": v(13.52, 6.15) * mm});
            skArc(sketch, "E61", {"start": v(13.52, 6.15) * mm, "mid": v(12.2, 7.2) * mm, "end": v(10.9, 6.14) * mm});
            skLineSegment(sketch, "E62.1.0.0", {"start": v(17.21, 8.25) * mm, "end": v(17.21, 10.78) * mm});
            skLineSegment(sketch, "E62.1.0.1", {"start": v(18.05, 10.78) * mm, "end": v(18.05, 8.25) * mm});
            skLineSegment(sketch, "E62.1.0.2", {"start": v(16.78, 8.25) * mm, "end": v(15.94, 8.25) * mm});
            skLineSegment(sketch, "E62.1.0.3", {"start": v(15.94, 8.25) * mm, "end": v(15.94, 10.78) * mm});
            skLineSegment(sketch, "E62.1.0.4", {"start": v(16.78, 10.78) * mm, "end": v(16.78, 8.25) * mm});
            skLineSegment(sketch, "E62.1.0.5", {"start": v(15.5, 10.78) * mm, "end": v(15.5, 8.25) * mm});
            skLineSegment(sketch, "E62.1.0.6", {"start": v(14.67, 8.25) * mm, "end": v(14.67, 10.78) * mm});
            skLineSegment(sketch, "E62.1.0.7", {"start": v(15.1, 2.5) * mm, "end": v(17.71, 2.5) * mm});
            skLineSegment(sketch, "E62.1.0.8", {"start": v(15.28, 16.22) * mm, "end": v(15.28, 12.83) * mm});
            skLineSegment(sketch, "E62.1.0.9", {"start": v(15.28, 12.83) * mm, "end": v(17.44, 12.83) * mm});
            skPoint(sketch, "E62.1.0.10", {"position": v(17.63, 11.06) * mm});
            skLineSegment(sketch, "E62.1.0.11", {"start": v(15.1, 6.14) * mm, "end": v(15.1, 2.5) * mm});
            skLineSegment(sketch, "E62.1.0.12", {"start": v(15.28, 16.22) * mm, "end": v(17.44, 16.22) * mm});
            skPoint(sketch, "E62.1.0.13", {"position": v(16.36, 11.06) * mm});
            skLineSegment(sketch, "E62.1.0.14", {"start": v(17.71, 2.5) * mm, "end": v(17.71, 6.15) * mm});
            skLineSegment(sketch, "E62.1.0.15", {"start": v(17.44, 16.22) * mm, "end": v(17.44, 12.83) * mm});
            skPoint(sketch, "E62.1.0.16", {"position": v(15.09, 11.06) * mm});
            skLineSegment(sketch, "E62.1.0.17", {"start": v(16.36, 16.22) * mm, "end": v(16.36, 12.83) * mm, "construction": true});
            skArc(sketch, "E62.1.0.18", {"start": v(17.71, 6.15) * mm, "mid": v(16.4, 7.2) * mm, "end": v(15.1, 6.14) * mm});
            skArc(sketch, "E62.1.0.19", {"start": v(16.78, 10.78) * mm, "mid": v(16.36, 11.06) * mm, "end": v(15.94, 10.78) * mm});
            skLineSegment(sketch, "E62.1.0.20", {"start": v(17.21, 10.78) * mm, "end": v(17.21, 8.25) * mm});
            skLineSegment(sketch, "E62.1.0.21", {"start": v(15.5, 8.25) * mm, "end": v(15.5, 10.78) * mm});
            skArc(sketch, "E62.1.0.22", {"start": v(18.05, 10.78) * mm, "mid": v(17.63, 11.06) * mm, "end": v(17.21, 10.78) * mm});
            skLineSegment(sketch, "E62.1.0.23", {"start": v(18.05, 8.25) * mm, "end": v(17.21, 8.25) * mm});
            skArc(sketch, "E62.1.0.24", {"start": v(15.5, 10.78) * mm, "mid": v(15.09, 11.06) * mm, "end": v(14.67, 10.78) * mm});
            skLineSegment(sketch, "E62.1.0.25", {"start": v(15.5, 8.25) * mm, "end": v(14.67, 8.25) * mm});
            skLineSegment(sketch, "E62.1.0.26", {"start": v(14.67, 8.25) * mm, "end": v(15.94, 8.25) * mm, "construction": true});
            skLineSegment(sketch, "E62.2.0.0", {"start": v(21.4, 8.25) * mm, "end": v(21.4, 10.78) * mm});
            skLineSegment(sketch, "E62.2.0.1", {"start": v(22.24, 10.78) * mm, "end": v(22.24, 8.25) * mm});
            skLineSegment(sketch, "E62.2.0.2", {"start": v(20.97, 8.25) * mm, "end": v(20.13, 8.25) * mm});
            skLineSegment(sketch, "E62.2.0.3", {"start": v(20.13, 8.25) * mm, "end": v(20.13, 10.78) * mm});
            skLineSegment(sketch, "E62.2.0.4", {"start": v(20.97, 10.78) * mm, "end": v(20.97, 8.25) * mm});
            skLineSegment(sketch, "E62.2.0.5", {"start": v(19.7, 10.78) * mm, "end": v(19.7, 8.25) * mm});
            skLineSegment(sketch, "E62.2.0.6", {"start": v(18.86, 8.25) * mm, "end": v(18.86, 10.78) * mm});
            skLineSegment(sketch, "E62.2.0.7", {"start": v(19.28, 2.5) * mm, "end": v(21.9, 2.5) * mm});
            skLineSegment(sketch, "E62.2.0.8", {"start": v(19.47, 16.22) * mm, "end": v(19.47, 12.83) * mm});
            skLineSegment(sketch, "E62.2.0.9", {"start": v(19.47, 12.83) * mm, "end": v(21.63, 12.83) * mm});
            skPoint(sketch, "E62.2.0.10", {"position": v(21.82, 11.06) * mm});
            skLineSegment(sketch, "E62.2.0.11", {"start": v(19.28, 6.14) * mm, "end": v(19.28, 2.5) * mm});
            skLineSegment(sketch, "E62.2.0.12", {"start": v(19.47, 16.22) * mm, "end": v(21.63, 16.22) * mm});
            skPoint(sketch, "E62.2.0.13", {"position": v(20.55, 11.06) * mm});
            skLineSegment(sketch, "E62.2.0.14", {"start": v(21.9, 2.5) * mm, "end": v(21.9, 6.15) * mm});
            skLineSegment(sketch, "E62.2.0.15", {"start": v(21.63, 16.22) * mm, "end": v(21.63, 12.83) * mm});
            skPoint(sketch, "E62.2.0.16", {"position": v(19.28, 11.06) * mm});
            skLineSegment(sketch, "E62.2.0.17", {"start": v(20.55, 16.22) * mm, "end": v(20.55, 12.83) * mm, "construction": true});
            skArc(sketch, "E62.2.0.18", {"start": v(21.9, 6.15) * mm, "mid": v(20.59, 7.2) * mm, "end": v(19.28, 6.14) * mm});
            skArc(sketch, "E62.2.0.19", {"start": v(20.97, 10.78) * mm, "mid": v(20.55, 11.06) * mm, "end": v(20.13, 10.78) * mm});
            skLineSegment(sketch, "E62.2.0.20", {"start": v(21.4, 10.78) * mm, "end": v(21.4, 8.25) * mm});
            skLineSegment(sketch, "E62.2.0.21", {"start": v(19.7, 8.25) * mm, "end": v(19.7, 10.78) * mm});
            skArc(sketch, "E62.2.0.22", {"start": v(22.24, 10.78) * mm, "mid": v(21.82, 11.06) * mm, "end": v(21.4, 10.78) * mm});
            skLineSegment(sketch, "E62.2.0.23", {"start": v(22.24, 8.25) * mm, "end": v(21.4, 8.25) * mm});
            skArc(sketch, "E62.2.0.24", {"start": v(19.7, 10.78) * mm, "mid": v(19.28, 11.06) * mm, "end": v(18.86, 10.78) * mm});
            skLineSegment(sketch, "E62.2.0.25", {"start": v(19.7, 8.25) * mm, "end": v(18.86, 8.25) * mm});
            skLineSegment(sketch, "E62.2.0.26", {"start": v(18.86, 8.25) * mm, "end": v(20.13, 8.25) * mm, "construction": true});
            skLineSegment(sketch, "E62.3.0.0", {"start": v(25.6, 8.25) * mm, "end": v(25.6, 10.78) * mm});
            skLineSegment(sketch, "E62.3.0.1", {"start": v(26.43, 10.78) * mm, "end": v(26.43, 8.25) * mm});
            skLineSegment(sketch, "E62.3.0.2", {"start": v(25.16, 8.25) * mm, "end": v(24.32, 8.25) * mm});
            skLineSegment(sketch, "E62.3.0.3", {"start": v(24.32, 8.25) * mm, "end": v(24.32, 10.78) * mm});
            skLineSegment(sketch, "E62.3.0.4", {"start": v(25.16, 10.78) * mm, "end": v(25.16, 8.25) * mm});
            skLineSegment(sketch, "E62.3.0.5", {"start": v(23.89, 10.78) * mm, "end": v(23.89, 8.25) * mm});
            skLineSegment(sketch, "E62.3.0.6", {"start": v(23.05, 8.25) * mm, "end": v(23.05, 10.78) * mm});
            skLineSegment(sketch, "E62.3.0.8", {"start": v(23.66, 16.22) * mm, "end": v(23.66, 12.83) * mm});
            skLineSegment(sketch, "E62.3.0.9", {"start": v(23.66, 12.83) * mm, "end": v(25.82, 12.83) * mm});
            skPoint(sketch, "E62.3.0.10", {"position": v(26.01, 11.06) * mm});
            skLineSegment(sketch, "E62.3.0.12", {"start": v(23.66, 16.22) * mm, "end": v(25.82, 16.22) * mm});
            skPoint(sketch, "E62.3.0.13", {"position": v(24.74, 11.06) * mm});
            skLineSegment(sketch, "E62.3.0.15", {"start": v(25.82, 16.22) * mm, "end": v(25.82, 12.83) * mm});
            skPoint(sketch, "E62.3.0.16", {"position": v(23.47, 11.06) * mm});
            skLineSegment(sketch, "E62.3.0.17", {"start": v(24.74, 16.22) * mm, "end": v(24.74, 12.83) * mm, "construction": true});
            skArc(sketch, "E62.3.0.19", {"start": v(25.16, 10.78) * mm, "mid": v(24.74, 11.06) * mm, "end": v(24.32, 10.78) * mm});
            skLineSegment(sketch, "E62.3.0.20", {"start": v(25.6, 10.78) * mm, "end": v(25.6, 8.25) * mm});
            skLineSegment(sketch, "E62.3.0.21", {"start": v(23.89, 8.25) * mm, "end": v(23.89, 10.78) * mm});
            skArc(sketch, "E62.3.0.22", {"start": v(26.43, 10.78) * mm, "mid": v(26.01, 11.06) * mm, "end": v(25.6, 10.78) * mm});
            skLineSegment(sketch, "E62.3.0.23", {"start": v(26.43, 8.25) * mm, "end": v(25.6, 8.25) * mm});
            skArc(sketch, "E62.3.0.24", {"start": v(23.89, 10.78) * mm, "mid": v(23.47, 11.06) * mm, "end": v(23.05, 10.78) * mm});
            skLineSegment(sketch, "E62.3.0.25", {"start": v(23.89, 8.25) * mm, "end": v(23.05, 8.25) * mm});
            skLineSegment(sketch, "E62.3.0.26", {"start": v(23.05, 8.25) * mm, "end": v(24.32, 8.25) * mm, "construction": true});
            skLineSegment(sketch, "E62.4.0.0", {"start": v(29.79, 8.25) * mm, "end": v(29.79, 10.78) * mm});
            skLineSegment(sketch, "E62.4.0.1", {"start": v(30.62, 10.78) * mm, "end": v(30.62, 8.25) * mm});
            skLineSegment(sketch, "E62.4.0.2", {"start": v(29.35, 8.25) * mm, "end": v(28.52, 8.25) * mm});
            skLineSegment(sketch, "E62.4.0.3", {"start": v(28.52, 8.25) * mm, "end": v(28.52, 10.78) * mm});
            skLineSegment(sketch, "E62.4.0.4", {"start": v(29.35, 10.78) * mm, "end": v(29.35, 8.25) * mm});
            skLineSegment(sketch, "E62.4.0.5", {"start": v(28.08, 10.78) * mm, "end": v(28.08, 8.25) * mm});
            skLineSegment(sketch, "E62.4.0.6", {"start": v(27.25, 8.25) * mm, "end": v(27.25, 10.78) * mm});
            skLineSegment(sketch, "E62.4.0.7", {"start": v(27.66, 2.5) * mm, "end": v(30.28, 2.5) * mm});
            skLineSegment(sketch, "E62.4.0.8", {"start": v(27.85, 16.22) * mm, "end": v(27.85, 12.83) * mm});
            skLineSegment(sketch, "E62.4.0.9", {"start": v(27.85, 12.83) * mm, "end": v(30.01, 12.83) * mm});
            skPoint(sketch, "E62.4.0.10", {"position": v(30.2, 11.06) * mm});
            skLineSegment(sketch, "E62.4.0.11", {"start": v(27.66, 6.14) * mm, "end": v(27.66, 2.5) * mm});
            skLineSegment(sketch, "E62.4.0.12", {"start": v(27.85, 16.22) * mm, "end": v(30.01, 16.22) * mm});
            skPoint(sketch, "E62.4.0.13", {"position": v(28.93, 11.06) * mm});
            skLineSegment(sketch, "E62.4.0.14", {"start": v(30.28, 2.5) * mm, "end": v(30.28, 6.15) * mm});
            skLineSegment(sketch, "E62.4.0.15", {"start": v(30.01, 16.22) * mm, "end": v(30.01, 12.83) * mm});
            skPoint(sketch, "E62.4.0.16", {"position": v(27.66, 11.06) * mm});
            skLineSegment(sketch, "E62.4.0.17", {"start": v(28.93, 16.22) * mm, "end": v(28.93, 12.83) * mm, "construction": true});
            skArc(sketch, "E62.4.0.18", {"start": v(30.28, 6.15) * mm, "mid": v(28.97, 7.2) * mm, "end": v(27.66, 6.14) * mm});
            skArc(sketch, "E62.4.0.19", {"start": v(29.35, 10.78) * mm, "mid": v(28.93, 11.06) * mm, "end": v(28.52, 10.78) * mm});
            skLineSegment(sketch, "E62.4.0.20", {"start": v(29.78, 10.78) * mm, "end": v(29.78, 8.25) * mm});
            skLineSegment(sketch, "E62.4.0.21", {"start": v(28.08, 8.25) * mm, "end": v(28.08, 10.78) * mm});
            skArc(sketch, "E62.4.0.22", {"start": v(30.62, 10.78) * mm, "mid": v(30.2, 11.06) * mm, "end": v(29.79, 10.78) * mm});
            skLineSegment(sketch, "E62.4.0.23", {"start": v(30.62, 8.25) * mm, "end": v(29.79, 8.25) * mm});
            skArc(sketch, "E62.4.0.24", {"start": v(28.08, 10.78) * mm, "mid": v(27.66, 11.06) * mm, "end": v(27.25, 10.78) * mm});
            skLineSegment(sketch, "E62.4.0.25", {"start": v(28.08, 8.25) * mm, "end": v(27.25, 8.25) * mm});
            skLineSegment(sketch, "E62.4.0.26", {"start": v(27.25, 8.25) * mm, "end": v(28.52, 8.25) * mm, "construction": true});
            skLineSegment(sketch, "E62.5.0.0", {"start": v(33.98, 8.25) * mm, "end": v(33.98, 10.78) * mm});
            skLineSegment(sketch, "E62.5.0.1", {"start": v(34.81, 10.78) * mm, "end": v(34.81, 8.25) * mm});
            skLineSegment(sketch, "E62.5.0.2", {"start": v(33.54, 8.25) * mm, "end": v(32.7, 8.25) * mm});
            skLineSegment(sketch, "E62.5.0.3", {"start": v(32.7, 8.25) * mm, "end": v(32.7, 10.78) * mm});
            skLineSegment(sketch, "E62.5.0.4", {"start": v(33.54, 10.78) * mm, "end": v(33.54, 8.25) * mm});
            skLineSegment(sketch, "E62.5.0.5", {"start": v(32.27, 10.78) * mm, "end": v(32.27, 8.25) * mm});
            skLineSegment(sketch, "E62.5.0.6", {"start": v(31.44, 8.25) * mm, "end": v(31.44, 10.78) * mm});
            skLineSegment(sketch, "E62.5.0.7", {"start": v(31.86, 2.5) * mm, "end": v(34.47, 2.5) * mm});
            skLineSegment(sketch, "E62.5.0.8", {"start": v(32.04, 16.22) * mm, "end": v(32.04, 12.83) * mm});
            skLineSegment(sketch, "E62.5.0.9", {"start": v(32.04, 12.83) * mm, "end": v(34.2, 12.83) * mm});
            skPoint(sketch, "E62.5.0.10", {"position": v(34.4, 11.06) * mm});
            skLineSegment(sketch, "E62.5.0.11", {"start": v(31.86, 6.14) * mm, "end": v(31.86, 2.5) * mm});
            skLineSegment(sketch, "E62.5.0.12", {"start": v(32.04, 16.22) * mm, "end": v(34.2, 16.22) * mm});
            skPoint(sketch, "E62.5.0.13", {"position": v(33.12, 11.06) * mm});
            skLineSegment(sketch, "E62.5.0.14", {"start": v(34.47, 2.5) * mm, "end": v(34.47, 6.15) * mm});
            skLineSegment(sketch, "E62.5.0.15", {"start": v(34.2, 16.22) * mm, "end": v(34.2, 12.83) * mm});
            skPoint(sketch, "E62.5.0.16", {"position": v(31.85, 11.06) * mm});
            skLineSegment(sketch, "E62.5.0.17", {"start": v(33.12, 16.22) * mm, "end": v(33.12, 12.83) * mm, "construction": true});
            skArc(sketch, "E62.5.0.18", {"start": v(34.47, 6.15) * mm, "mid": v(33.16, 7.2) * mm, "end": v(31.86, 6.14) * mm});
            skArc(sketch, "E62.5.0.19", {"start": v(33.54, 10.78) * mm, "mid": v(33.12, 11.06) * mm, "end": v(32.7, 10.78) * mm});
            skLineSegment(sketch, "E62.5.0.20", {"start": v(33.98, 10.78) * mm, "end": v(33.98, 8.25) * mm});
            skLineSegment(sketch, "E62.5.0.21", {"start": v(32.27, 8.25) * mm, "end": v(32.27, 10.78) * mm});
            skArc(sketch, "E62.5.0.22", {"start": v(34.81, 10.78) * mm, "mid": v(34.4, 11.06) * mm, "end": v(33.98, 10.78) * mm});
            skLineSegment(sketch, "E62.5.0.23", {"start": v(34.81, 8.25) * mm, "end": v(33.98, 8.25) * mm});
            skArc(sketch, "E62.5.0.24", {"start": v(32.27, 10.78) * mm, "mid": v(31.85, 11.06) * mm, "end": v(31.44, 10.78) * mm});
            skLineSegment(sketch, "E62.5.0.25", {"start": v(32.27, 8.25) * mm, "end": v(31.44, 8.25) * mm});
            skLineSegment(sketch, "E62.5.0.26", {"start": v(31.44, 8.25) * mm, "end": v(32.7, 8.25) * mm, "construction": true});
            skLineSegment(sketch, "E62.direction1", {"start": v(10.9, 2.5) * mm, "end": v(15.1, 2.5) * mm, "construction": true});
            skLineSegment(sketch, "E63", {"start": v(22.67, 0) * mm, "end": v(22.67, 5.6) * mm});
            skLineSegment(sketch, "E64", {"start": v(22.67, 5.6) * mm, "end": v(26.76, 5.6) * mm});
            skLineSegment(sketch, "E65", {"start": v(26.76, 5.6) * mm, "end": v(26.76, 0) * mm});
            skLineSegment(sketch, "E66", {"start": v(26.76, 0) * mm, "end": v(22.67, 0) * mm});
            skSolve(sketch);
        }
        {
            var Q0;
            Q0 = qSketchRegion(id + "F11", true);
            extrude(context, id + "F12", {"entities" : qUnion([Q0]), "operationType" : NewBodyOperationType.REMOVE, "oppositeDirection" : true, "depth" : 1.27 * mm, "offsetDistance" : 25.4 * mm});
        }
        {
            var Q0;
            Q0=makeQuery(id+"F3.boolean.opBoolean","MERGE",FACE,{"derivedFrom":[makeQuery(id+"F1.opExtrude","SWEPT_FACE",FACE,{"disambiguationData":[OSD([sQuery(id+"F0.wireOp",EDGE,"E4")])]}),makeQuery(id+"F3.opExtrude","SWEPT_FACE",FACE,{"disambiguationData":[OSD([sQuery(id+"F2.wireOp",EDGE,"E6")])]})]});
            var sketch = newSketch(context, id + "F13", { "sketchPlane" : qUnion([Q0])});
            skLineSegment(sketch, "E67.4.0.0", {"start": v(26.32, 8.45) * mm, "end": v(26.32, 10.99) * mm});
            skLineSegment(sketch, "E67.4.0.1", {"start": v(27.15, 10.99) * mm, "end": v(27.15, 8.45) * mm});
            skLineSegment(sketch, "E67.4.0.2", {"start": v(25.88, 8.45) * mm, "end": v(25.05, 8.45) * mm});
            skLineSegment(sketch, "E67.4.0.3", {"start": v(25.05, 8.45) * mm, "end": v(25.05, 10.99) * mm});
            skLineSegment(sketch, "E67.4.0.4", {"start": v(25.88, 10.99) * mm, "end": v(25.88, 8.45) * mm});
            skLineSegment(sketch, "E67.4.0.5", {"start": v(24.61, 10.99) * mm, "end": v(24.61, 8.45) * mm});
            skLineSegment(sketch, "E67.4.0.6", {"start": v(23.78, 8.45) * mm, "end": v(23.78, 10.99) * mm});
            skLineSegment(sketch, "E67.4.0.7", {"start": v(24.2, 2.71) * mm, "end": v(26.82, 2.71) * mm});
            skLineSegment(sketch, "E67.4.0.8", {"start": v(24.39, 16.42) * mm, "end": v(24.39, 13.03) * mm});
            skLineSegment(sketch, "E67.4.0.9", {"start": v(24.39, 13.03) * mm, "end": v(26.55, 13.03) * mm});
            skPoint(sketch, "E67.4.0.10", {"position": v(26.74, 11.26) * mm});
            skLineSegment(sketch, "E67.4.0.11", {"start": v(24.2, 6.34) * mm, "end": v(24.2, 2.71) * mm});
            skLineSegment(sketch, "E67.4.0.12", {"start": v(24.39, 16.42) * mm, "end": v(26.55, 16.42) * mm});
            skPoint(sketch, "E67.4.0.13", {"position": v(25.47, 11.26) * mm});
            skLineSegment(sketch, "E67.4.0.14", {"start": v(26.82, 2.71) * mm, "end": v(26.82, 6.36) * mm});
            skLineSegment(sketch, "E67.4.0.15", {"start": v(26.55, 16.42) * mm, "end": v(26.55, 13.03) * mm});
            skPoint(sketch, "E67.4.0.16", {"position": v(24.2, 11.26) * mm});
            skLineSegment(sketch, "E67.4.0.17", {"start": v(25.47, 16.42) * mm, "end": v(25.47, 13.03) * mm, "construction": true});
            skArc(sketch, "E67.4.0.18", {"start": v(26.82, 6.36) * mm, "mid": v(25.5, 7.4) * mm, "end": v(24.2, 6.34) * mm});
            skArc(sketch, "E67.4.0.19", {"start": v(25.88, 10.99) * mm, "mid": v(25.47, 11.26) * mm, "end": v(25.05, 10.99) * mm});
            skLineSegment(sketch, "E67.4.0.20", {"start": v(26.32, 10.99) * mm, "end": v(26.32, 8.45) * mm});
            skLineSegment(sketch, "E67.4.0.21", {"start": v(24.61, 8.45) * mm, "end": v(24.61, 10.99) * mm});
            skArc(sketch, "E67.4.0.22", {"start": v(27.15, 10.99) * mm, "mid": v(26.74, 11.26) * mm, "end": v(26.32, 10.99) * mm});
            skLineSegment(sketch, "E67.4.0.23", {"start": v(27.15, 8.45) * mm, "end": v(26.32, 8.45) * mm});
            skArc(sketch, "E67.4.0.24", {"start": v(24.61, 10.99) * mm, "mid": v(24.2, 11.26) * mm, "end": v(23.78, 10.99) * mm});
            skLineSegment(sketch, "E67.4.0.25", {"start": v(24.61, 8.45) * mm, "end": v(23.78, 8.45) * mm});
            skLineSegment(sketch, "E67.4.0.26", {"start": v(23.78, 8.45) * mm, "end": v(25.05, 8.45) * mm, "construction": true});
            skLineSegment(sketch, "E67.5.0.0", {"start": v(30.51, 8.45) * mm, "end": v(30.51, 10.99) * mm});
            skLineSegment(sketch, "E67.5.0.1", {"start": v(31.35, 10.99) * mm, "end": v(31.35, 8.45) * mm});
            skLineSegment(sketch, "E67.5.0.2", {"start": v(30.08, 8.45) * mm, "end": v(29.24, 8.45) * mm});
            skLineSegment(sketch, "E67.5.0.3", {"start": v(29.24, 8.45) * mm, "end": v(29.24, 10.99) * mm});
            skLineSegment(sketch, "E67.5.0.4", {"start": v(30.08, 10.99) * mm, "end": v(30.08, 8.45) * mm});
            skLineSegment(sketch, "E67.5.0.5", {"start": v(28.8, 10.99) * mm, "end": v(28.8, 8.45) * mm});
            skLineSegment(sketch, "E67.5.0.6", {"start": v(27.97, 8.45) * mm, "end": v(27.97, 10.99) * mm});
            skLineSegment(sketch, "E67.5.0.7", {"start": v(28.4, 2.71) * mm, "end": v(31, 2.71) * mm});
            skLineSegment(sketch, "E67.5.0.8", {"start": v(28.58, 16.42) * mm, "end": v(28.58, 13.03) * mm});
            skLineSegment(sketch, "E67.5.0.9", {"start": v(28.58, 13.03) * mm, "end": v(30.74, 13.03) * mm});
            skPoint(sketch, "E67.5.0.10", {"position": v(30.93, 11.26) * mm});
            skLineSegment(sketch, "E67.5.0.11", {"start": v(28.4, 6.34) * mm, "end": v(28.4, 2.71) * mm});
            skLineSegment(sketch, "E67.5.0.12", {"start": v(28.58, 16.42) * mm, "end": v(30.74, 16.42) * mm});
            skPoint(sketch, "E67.5.0.13", {"position": v(29.66, 11.26) * mm});
            skLineSegment(sketch, "E67.5.0.14", {"start": v(31, 2.71) * mm, "end": v(31, 6.36) * mm});
            skLineSegment(sketch, "E67.5.0.15", {"start": v(30.74, 16.42) * mm, "end": v(30.74, 13.03) * mm});
            skPoint(sketch, "E67.5.0.16", {"position": v(28.39, 11.26) * mm});
            skLineSegment(sketch, "E67.5.0.17", {"start": v(29.66, 16.42) * mm, "end": v(29.66, 13.03) * mm, "construction": true});
            skArc(sketch, "E67.5.0.18", {"start": v(31, 6.36) * mm, "mid": v(29.7, 7.4) * mm, "end": v(28.4, 6.34) * mm});
            skArc(sketch, "E67.5.0.19", {"start": v(30.08, 10.99) * mm, "mid": v(29.66, 11.26) * mm, "end": v(29.24, 10.99) * mm});
            skLineSegment(sketch, "E67.5.0.20", {"start": v(30.51, 10.99) * mm, "end": v(30.51, 8.45) * mm});
            skLineSegment(sketch, "E67.5.0.21", {"start": v(28.8, 8.45) * mm, "end": v(28.8, 10.99) * mm});
            skArc(sketch, "E67.5.0.22", {"start": v(31.35, 10.99) * mm, "mid": v(30.93, 11.26) * mm, "end": v(30.51, 10.99) * mm});
            skLineSegment(sketch, "E67.5.0.23", {"start": v(31.35, 8.45) * mm, "end": v(30.51, 8.45) * mm});
            skArc(sketch, "E67.5.0.24", {"start": v(28.8, 10.99) * mm, "mid": v(28.39, 11.26) * mm, "end": v(27.97, 10.99) * mm});
            skLineSegment(sketch, "E67.5.0.25", {"start": v(28.8, 8.45) * mm, "end": v(27.97, 8.45) * mm});
            skLineSegment(sketch, "E67.5.0.26", {"start": v(27.97, 8.45) * mm, "end": v(29.24, 8.45) * mm, "construction": true});
            skLineSegment(sketch, "E68.1.0.0", {"start": v(33.48, 8.45) * mm, "end": v(33.48, 10.99) * mm});
            skLineSegment(sketch, "E68.1.0.1", {"start": v(34.75, 8.45) * mm, "end": v(33.92, 8.45) * mm});
            skArc(sketch, "E68.1.0.2", {"start": v(33.48, 10.99) * mm, "mid": v(33.06, 11.26) * mm, "end": v(32.65, 10.99) * mm});
            skLineSegment(sketch, "E68.1.0.3", {"start": v(33.48, 10.99) * mm, "end": v(33.48, 8.45) * mm});
            skPoint(sketch, "E68.1.0.4", {"position": v(35.6, 11.26) * mm});
            skArc(sketch, "E68.1.0.5", {"start": v(36.02, 10.99) * mm, "mid": v(35.6, 11.26) * mm, "end": v(35.19, 10.99) * mm});
            skLineSegment(sketch, "E68.1.0.6", {"start": v(33.92, 8.45) * mm, "end": v(33.92, 10.99) * mm});
            skLineSegment(sketch, "E68.1.0.7", {"start": v(32.65, 8.45) * mm, "end": v(32.65, 10.99) * mm});
            skPoint(sketch, "E68.1.0.8", {"position": v(34.33, 11.26) * mm});
            skLineSegment(sketch, "E68.1.0.9", {"start": v(36.02, 8.45) * mm, "end": v(35.19, 8.45) * mm});
            skLineSegment(sketch, "E68.1.0.10", {"start": v(34.75, 10.99) * mm, "end": v(34.75, 8.45) * mm});
            skLineSegment(sketch, "E68.1.0.11", {"start": v(35.19, 8.45) * mm, "end": v(35.19, 10.99) * mm});
            skArc(sketch, "E68.1.0.12", {"start": v(34.75, 10.99) * mm, "mid": v(34.33, 11.26) * mm, "end": v(33.92, 10.99) * mm});
            skLineSegment(sketch, "E68.1.0.13", {"start": v(32.65, 8.45) * mm, "end": v(33.92, 8.45) * mm, "construction": true});
            skPoint(sketch, "E68.1.0.14", {"position": v(33.06, 11.26) * mm});
            skLineSegment(sketch, "E68.1.0.15", {"start": v(35.18, 10.99) * mm, "end": v(35.18, 8.45) * mm});
            skLineSegment(sketch, "E68.1.0.16", {"start": v(36.02, 10.99) * mm, "end": v(36.02, 8.45) * mm});
            skLineSegment(sketch, "E68.1.0.17", {"start": v(33.48, 8.45) * mm, "end": v(32.65, 8.45) * mm});
            skLineSegment(sketch, "E68.direction1", {"start": v(27.97, 8.45) * mm, "end": v(32.65, 8.45) * mm, "construction": true});
            skLineSegment(sketch, "E69", {"start": v(32.23, 0) * mm, "end": v(32.23, 5.36) * mm});
            skLineSegment(sketch, "E70", {"start": v(35.66, 5.36) * mm, "end": v(35.66, 0) * mm});
            skLineSegment(sketch, "E71", {"start": v(35.66, 0) * mm, "end": v(32.23, 0) * mm});
            skArc(sketch, "E72", {"start": v(35.66, 5.36) * mm, "mid": v(33.94, 7.07) * mm, "end": v(32.23, 5.36) * mm});
            skSolve(sketch);
        }
        {
            var Q0;
            Q0 = qSketchRegion(id + "F13", true);
            extrude(context, id + "F14", {"entities" : qUnion([Q0]), "operationType" : NewBodyOperationType.REMOVE, "oppositeDirection" : true, "depth" : 1.27 * mm, "offsetDistance" : 25.4 * mm});
        }
        {
            var Q0;
            Q0=makeQuery(id+"F1.opExtrude","SWEPT_FACE",FACE,{"disambiguationData":[OSD([sQuery(id+"F0.wireOp",EDGE,"E3")])]});
            var sketch = newSketch(context, id + "F15", { "sketchPlane" : qUnion([Q0])});
            skLineSegment(sketch, "E73", {"start": v(-8.8, 13.2) * mm, "end": v(-8.8, 0) * mm});
            skLineSegment(sketch, "E74", {"start": v(-8.8, 0) * mm, "end": v(-8.08, 0) * mm});
            skLineSegment(sketch, "E75", {"start": v(-8.08, 0) * mm, "end": v(-8.08, 13.2) * mm});
            skLineSegment(sketch, "E76", {"start": v(-8.08, 13.2) * mm, "end": v(-8.8, 13.2) * mm});
            skLineSegment(sketch, "E77.1.0.0", {"start": v(-4.5, 0) * mm, "end": v(-4.5, 13.2) * mm});
            skLineSegment(sketch, "E77.1.0.1", {"start": v(-5.22, 13.2) * mm, "end": v(-5.22, 0) * mm});
            skLineSegment(sketch, "E77.1.0.2", {"start": v(-4.5, 13.2) * mm, "end": v(-5.22, 13.2) * mm});
            skLineSegment(sketch, "E77.1.0.3", {"start": v(-5.22, 0) * mm, "end": v(-4.5, 0) * mm});
            skLineSegment(sketch, "E77.2.0.0", {"start": v(-0.92, 0) * mm, "end": v(-0.92, 13.2) * mm});
            skLineSegment(sketch, "E77.2.0.1", {"start": v(-1.64, 13.2) * mm, "end": v(-1.64, 0) * mm});
            skLineSegment(sketch, "E77.2.0.2", {"start": v(-0.92, 13.2) * mm, "end": v(-1.64, 13.2) * mm});
            skLineSegment(sketch, "E77.2.0.3", {"start": v(-1.64, 0) * mm, "end": v(-0.92, 0) * mm});
            skLineSegment(sketch, "E77.3.0.0", {"start": v(2.66, 0) * mm, "end": v(2.66, 13.2) * mm});
            skLineSegment(sketch, "E77.3.0.1", {"start": v(1.94, 13.2) * mm, "end": v(1.94, 0) * mm});
            skLineSegment(sketch, "E77.3.0.2", {"start": v(2.66, 13.2) * mm, "end": v(1.94, 13.2) * mm});
            skLineSegment(sketch, "E77.3.0.3", {"start": v(1.94, 0) * mm, "end": v(2.66, 0) * mm});
            skLineSegment(sketch, "E77.4.0.0", {"start": v(6.24, 0) * mm, "end": v(6.24, 13.2) * mm});
            skLineSegment(sketch, "E77.4.0.1", {"start": v(5.53, 13.2) * mm, "end": v(5.53, 0) * mm});
            skLineSegment(sketch, "E77.4.0.2", {"start": v(6.24, 13.2) * mm, "end": v(5.53, 13.2) * mm});
            skLineSegment(sketch, "E77.4.0.3", {"start": v(5.53, 0) * mm, "end": v(6.24, 0) * mm});
            skLineSegment(sketch, "E77.5.0.0", {"start": v(9.82, 0) * mm, "end": v(9.82, 13.2) * mm});
            skLineSegment(sketch, "E77.5.0.1", {"start": v(9.1, 13.2) * mm, "end": v(9.1, 0) * mm});
            skLineSegment(sketch, "E77.5.0.2", {"start": v(9.82, 13.2) * mm, "end": v(9.1, 13.2) * mm});
            skLineSegment(sketch, "E77.5.0.3", {"start": v(9.1, 0) * mm, "end": v(9.82, 0) * mm});
            skLineSegment(sketch, "E77.6.0.0", {"start": v(13.4, 0) * mm, "end": v(13.4, 13.2) * mm});
            skLineSegment(sketch, "E77.6.0.1", {"start": v(12.69, 13.2) * mm, "end": v(12.69, 0) * mm});
            skLineSegment(sketch, "E77.6.0.2", {"start": v(13.4, 13.2) * mm, "end": v(12.69, 13.2) * mm});
            skLineSegment(sketch, "E77.6.0.3", {"start": v(12.69, 0) * mm, "end": v(13.4, 0) * mm});
            skLineSegment(sketch, "E77.direction1", {"start": v(-8.8, 0) * mm, "end": v(-5.22, 0) * mm, "construction": true});
            skSolve(sketch);
        }
        {
            var Q0;
            Q0 = qSketchRegion(id + "F15", true);
            extrude(context, id + "F16", {"entities" : qUnion([Q0]), "operationType" : NewBodyOperationType.ADD, "depth" : 0.79 * mm, "offsetDistance" : 25.4 * mm});
        }
        {
            var Q0;
            Q0=makeQuery(id+"F3.opExtrude","CAP_FACE",FACE,{"disambiguationData":[OSD([sQuery(id+"F2.wireOp",EDGE,"E5"),sQuery(id+"F2.wireOp",EDGE,"E6"),sQuery(id+"F2.wireOp",EDGE,"E7"),sQuery(id+"F2.wireOp",EDGE,"E8"),sQuery(id+"F2.wireOp",EDGE,"E9")])],"isStart":false});
            var sketch = newSketch(context, id + "F17", { "sketchPlane" : qUnion([Q0])});
            skCircle(sketch, "E78", {"center": v(-1.48, -23.37) * mm, "radius": 3.23 * mm});
            skSolve(sketch);
        }
        {
            var Q0;
            Q0=makeQuery(id+"F17.imprint","IMPRINT",FACE,{"disambiguationData":[TD([[makeQuery(id+"F17.imprint","IMPRINT",EDGE,{"derivedFrom":sQuery(id+"F17.wireOp",EDGE,"E78")}),-1.0]])]});
            var sketch = newSketch(context, id + "F18", { "sketchPlane" : qUnion([Q0])});
            skLineSegment(sketch, "E79", {"start": v(4.78, 15.72) * mm, "end": v(3.65, 15.92) * mm});
            skLineSegment(sketch, "E80", {"start": v(2.64, 15.92) * mm, "end": v(2.64, 17.32) * mm});
            skLineSegment(sketch, "E81", {"start": v(2.64, 20.03) * mm, "end": v(1.4, 20.03) * mm});
            skLineSegment(sketch, "E82", {"start": v(1.4, 20.03) * mm, "end": v(1.4, 19.03) * mm});
            skLineSegment(sketch, "E83", {"start": v(1.4, 15.92) * mm, "end": v(2.64, 15.92) * mm});
            skLineSegment(sketch, "E84", {"start": v(3.65, 17.32) * mm, "end": v(2.64, 17.32) * mm});
            skLineSegment(sketch, "E85", {"start": v(-2.85, 17.32) * mm, "end": v(-2.85, 19.03) * mm});
            skLineSegment(sketch, "E86", {"start": v(-2.85, 19.03) * mm, "end": v(1.4, 19.03) * mm});
            skLineSegment(sketch, "E87", {"start": v(1.4, 9.4) * mm, "end": v(-2.85, 9.4) * mm});
            skLineSegment(sketch, "E88", {"start": v(-2.85, 9.4) * mm, "end": v(-2.85, 7.52) * mm});
            skLineSegment(sketch, "E89", {"start": v(-2.85, 7.52) * mm, "end": v(1.4, 7.52) * mm});
            skLineSegment(sketch, "E90", {"start": v(1.4, 5.5) * mm, "end": v(-2.85, 5.5) * mm});
            skLineSegment(sketch, "E91", {"start": v(-2.85, 5.5) * mm, "end": v(-2.85, 3.74) * mm});
            skLineSegment(sketch, "E92", {"start": v(-2.85, 3.74) * mm, "end": v(1.4, 3.74) * mm});
            skLineSegment(sketch, "E93", {"start": v(1.1, 2.13) * mm, "end": v(-2.85, 2.13) * mm});
            skLineSegment(sketch, "E94", {"start": v(-2.85, 2.13) * mm, "end": v(-2.85, 0.4) * mm});
            skLineSegment(sketch, "E95", {"start": v(-2.85, 0.4) * mm, "end": v(1.4, 0.4) * mm});
            skLineSegment(sketch, "E96", {"start": v(1.07, -1.17) * mm, "end": v(-2.85, -1.17) * mm});
            skLineSegment(sketch, "E97", {"start": v(-2.85, -1.17) * mm, "end": v(-2.85, -2.98) * mm});
            skLineSegment(sketch, "E98", {"start": v(-2.85, -2.98) * mm, "end": v(1.36, -2.98) * mm});
            skLineSegment(sketch, "E99", {"start": v(4.75, -4.04) * mm, "end": v(-2.13, -4.04) * mm});
            skLineSegment(sketch, "E100", {"start": v(-2.13, -4.82) * mm, "end": v(4.9, -4.82) * mm});
            skLineSegment(sketch, "E101", {"start": v(4.9, -4.82) * mm, "end": v(4.75, -4.04) * mm});
            skLineSegment(sketch, "E102", {"start": v(4.75, -11.75) * mm, "end": v(-2.13, -11.75) * mm});
            skLineSegment(sketch, "E103", {"start": v(-2.13, -12.55) * mm, "end": v(1.84, -12.55) * mm});
            skLineSegment(sketch, "E104", {"start": v(5, -12.55) * mm, "end": v(4.75, -11.75) * mm});
            skLineSegment(sketch, "E105", {"start": v(3.65, 17.32) * mm, "end": v(3.73, 17.07) * mm});
            skLineSegment(sketch, "E106", {"start": v(3.73, 17.07) * mm, "end": v(3.73, 16.2) * mm});
            skLineSegment(sketch, "E107", {"start": v(3.73, 16.2) * mm, "end": v(3.65, 15.92) * mm});
            skLineSegment(sketch, "E108", {"start": v(4.78, 15.72) * mm, "end": v(4.9, 15.99) * mm});
            skLineSegment(sketch, "E109", {"start": v(4.9, 15.99) * mm, "end": v(5.02, 16.7) * mm});
            skLineSegment(sketch, "E110", {"start": v(3.65, 19.03) * mm, "end": v(3.88, 18.97) * mm});
            skLineSegment(sketch, "E111", {"start": v(3.88, 18.97) * mm, "end": v(4.53, 18.64) * mm});
            skLineSegment(sketch, "E112", {"start": v(4.53, 18.64) * mm, "end": v(4.94, 17.92) * mm});
            skLineSegment(sketch, "E113", {"start": v(4.94, 17.92) * mm, "end": v(5.03, 17.33) * mm});
            skLineSegment(sketch, "E114", {"start": v(5.03, 17.33) * mm, "end": v(5.02, 16.7) * mm});
            skLineSegment(sketch, "E115", {"start": v(0.92, 13.61) * mm, "end": v(-1.22, 13.61) * mm});
            skArc(sketch, "E116", {"start": v(-1.22, 13.61) * mm, "mid": v(-1.86, 12.8) * mm, "end": v(-1.22, 12) * mm});
            skLineSegment(sketch, "E117", {"start": v(-1.22, 12) * mm, "end": v(0.9, 12) * mm});
            skArc(sketch, "E118", {"start": v(0.9, 12) * mm, "mid": v(1.58, 12.8) * mm, "end": v(0.92, 13.61) * mm});
            skLineSegment(sketch, "E119", {"start": v(0.76, 12.8) * mm, "end": v(3.87, 12.8) * mm, "construction": true});
            skLineSegment(sketch, "E120", {"start": v(0, 12.8) * mm, "end": v(0, 9.82) * mm, "construction": true});
            skArc(sketch, "E121.MirrorCS", {"start": v(0.9, 13.61) * mm, "mid": v(1.58, 12.8) * mm, "end": v(0.92, 12) * mm});
            skLineSegment(sketch, "E122.trimOffspring", {"start": v(2.64, 19.03) * mm, "end": v(2.64, 20.03) * mm});
            skLineSegment(sketch, "E123.trimOffspring", {"start": v(2.64, 19.03) * mm, "end": v(3.65, 19.03) * mm});
            skLineSegment(sketch, "E124.trimOffspring", {"start": v(1.4, 17.32) * mm, "end": v(-2.85, 17.32) * mm});
            skLineSegment(sketch, "E125.trimOffspring", {"start": v(1.4, 17.32) * mm, "end": v(1.4, 15.92) * mm});
            skLineSegment(sketch, "E126", {"start": v(1.4, 7.52) * mm, "end": v(1.4, 6.18) * mm});
            skLineSegment(sketch, "E127", {"start": v(1.4, 6.18) * mm, "end": v(2.7, 6.18) * mm});
            skLineSegment(sketch, "E128", {"start": v(2.7, 6.18) * mm, "end": v(2.7, 7.25) * mm});
            skLineSegment(sketch, "E129", {"start": v(2.7, 7.25) * mm, "end": v(2.66, 7.88) * mm});
            skLineSegment(sketch, "E130", {"start": v(2.66, 7.88) * mm, "end": v(2.5, 8.87) * mm});
            skLineSegment(sketch, "E131", {"start": v(2.5, 8.87) * mm, "end": v(2.36, 9.1) * mm});
            skLineSegment(sketch, "E132", {"start": v(2.36, 9.1) * mm, "end": v(2.24, 9.26) * mm});
            skLineSegment(sketch, "E133", {"start": v(2.24, 9.26) * mm, "end": v(2.08, 9.4) * mm});
            skLineSegment(sketch, "E134", {"start": v(2.08, 9.4) * mm, "end": v(1.4, 9.4) * mm});
            skLineSegment(sketch, "E135", {"start": v(1.4, 5.5) * mm, "end": v(2.06, 5.5) * mm});
            skLineSegment(sketch, "E136", {"start": v(2.06, 5.5) * mm, "end": v(2.33, 5.26) * mm});
            skLineSegment(sketch, "E137", {"start": v(2.33, 5.26) * mm, "end": v(2.57, 4.45) * mm});
            skLineSegment(sketch, "E138", {"start": v(2.57, 4.45) * mm, "end": v(2.72, 3.46) * mm});
            skLineSegment(sketch, "E139", {"start": v(2.72, 3.46) * mm, "end": v(2.72, 2.22) * mm});
            skLineSegment(sketch, "E140", {"start": v(2.72, 2.22) * mm, "end": v(2.61, 1.62) * mm});
            skLineSegment(sketch, "E141", {"start": v(2.61, 1.62) * mm, "end": v(2.33, 1.13) * mm});
            skLineSegment(sketch, "E142", {"start": v(2.33, 1.13) * mm, "end": v(2.55, 0.76) * mm});
            skLineSegment(sketch, "E143", {"start": v(2.55, 0.76) * mm, "end": v(2.69, 0) * mm});
            skLineSegment(sketch, "E144", {"start": v(2.69, 0) * mm, "end": v(2.75, -1.39) * mm});
            skLineSegment(sketch, "E145", {"start": v(2.75, -1.39) * mm, "end": v(2.63, -2.03) * mm});
            skLineSegment(sketch, "E146", {"start": v(2.63, -2.03) * mm, "end": v(2.38, -2.5) * mm});
            skLineSegment(sketch, "E147", {"start": v(2.38, -2.5) * mm, "end": v(2.23, -2.61) * mm});
            skLineSegment(sketch, "E148", {"start": v(2.23, -2.61) * mm, "end": v(1.7, -2.93) * mm});
            skLineSegment(sketch, "E149", {"start": v(1.7, -2.93) * mm, "end": v(1.36, -2.98) * mm});
            skLineSegment(sketch, "E150", {"start": v(1.4, 3.74) * mm, "end": v(1.58, 3.43) * mm});
            skLineSegment(sketch, "E151", {"start": v(1.58, 3.43) * mm, "end": v(1.61, 3.02) * mm});
            skLineSegment(sketch, "E152", {"start": v(1.61, 3.02) * mm, "end": v(1.58, 2.54) * mm});
            skLineSegment(sketch, "E153", {"start": v(1.58, 2.54) * mm, "end": v(1.35, 2.25) * mm});
            skLineSegment(sketch, "E154", {"start": v(1.35, 2.25) * mm, "end": v(1.1, 2.13) * mm});
            skLineSegment(sketch, "E155", {"start": v(1.4, 0.4) * mm, "end": v(1.58, 0.1) * mm});
            skLineSegment(sketch, "E156", {"start": v(1.58, 0.1) * mm, "end": v(1.62, -0.38) * mm});
            skLineSegment(sketch, "E157", {"start": v(1.62, -0.38) * mm, "end": v(1.57, -0.78) * mm});
            skLineSegment(sketch, "E158", {"start": v(1.57, -0.78) * mm, "end": v(1.33, -1.05) * mm});
            skLineSegment(sketch, "E159", {"start": v(1.33, -1.05) * mm, "end": v(1.07, -1.17) * mm});
            skLineSegment(sketch, "E160", {"start": v(-2.13, -4.04) * mm, "end": v(-2.56, -4.19) * mm});
            skLineSegment(sketch, "E161", {"start": v(-2.56, -4.19) * mm, "end": v(-2.92, -4.56) * mm});
            skLineSegment(sketch, "E162", {"start": v(-2.92, -4.56) * mm, "end": v(-2.97, -5.12) * mm});
            skLineSegment(sketch, "E163", {"start": v(-2.97, -5.12) * mm, "end": v(-2.92, -5.6) * mm});
            skLineSegment(sketch, "E164", {"start": v(-2.92, -5.6) * mm, "end": v(-2.79, -5.83) * mm});
            skLineSegment(sketch, "E165", {"start": v(-2.79, -5.83) * mm, "end": v(-2.22, -5.74) * mm});
            skLineSegment(sketch, "E166", {"start": v(-2.22, -5.74) * mm, "end": v(-2.32, -5.43) * mm});
            skLineSegment(sketch, "E167", {"start": v(-2.32, -5.43) * mm, "end": v(-2.32, -5.1) * mm});
            skLineSegment(sketch, "E168", {"start": v(-2.32, -5.1) * mm, "end": v(-2.13, -4.82) * mm});
            skLineSegment(sketch, "E169", {"start": v(2.38, -6.47) * mm, "end": v(1.74, -6.6) * mm});
            skLineSegment(sketch, "E170", {"start": v(1.74, -6.6) * mm, "end": v(1.9, -7.13) * mm});
            skLineSegment(sketch, "E171", {"start": v(1.9, -7.13) * mm, "end": v(2.05, -8) * mm});
            skLineSegment(sketch, "E172", {"start": v(2.05, -8) * mm, "end": v(2.05, -9.38) * mm});
            skLineSegment(sketch, "E173", {"start": v(2.05, -9.38) * mm, "end": v(1.8, -9.8) * mm});
            skLineSegment(sketch, "E174", {"start": v(1.8, -9.8) * mm, "end": v(1.49, -9.98) * mm});
            skLineSegment(sketch, "E175", {"start": v(1.49, -9.98) * mm, "end": v(0.7, -9.98) * mm});
            skLineSegment(sketch, "E176", {"start": v(0.7, -9.98) * mm, "end": v(0.28, -7.27) * mm});
            skLineSegment(sketch, "E177", {"start": v(0.28, -7.27) * mm, "end": v(0.12, -6.76) * mm});
            skLineSegment(sketch, "E178", {"start": v(0.12, -6.76) * mm, "end": v(-0.3, -6.36) * mm});
            skLineSegment(sketch, "E179", {"start": v(-0.3, -6.36) * mm, "end": v(-0.76, -6.24) * mm});
            skLineSegment(sketch, "E180", {"start": v(-0.76, -6.24) * mm, "end": v(-1.37, -6.24) * mm});
            skLineSegment(sketch, "E181", {"start": v(-1.37, -6.24) * mm, "end": v(-1.87, -6.24) * mm});
            skLineSegment(sketch, "E182", {"start": v(-1.87, -6.24) * mm, "end": v(-2.4, -6.56) * mm});
            skLineSegment(sketch, "E183", {"start": v(-2.4, -6.56) * mm, "end": v(-2.75, -7.04) * mm});
            skLineSegment(sketch, "E184", {"start": v(-2.75, -7.04) * mm, "end": v(-2.92, -7.63) * mm});
            skLineSegment(sketch, "E185", {"start": v(-2.92, -7.63) * mm, "end": v(-2.96, -8.62) * mm});
            skLineSegment(sketch, "E186", {"start": v(-2.96, -8.62) * mm, "end": v(-2.84, -9.8) * mm});
            skLineSegment(sketch, "E187", {"start": v(-2.84, -9.8) * mm, "end": v(-2.64, -10.46) * mm});
            skLineSegment(sketch, "E188", {"start": v(-2.64, -10.46) * mm, "end": v(-2.38, -10.7) * mm});
            skLineSegment(sketch, "E189", {"start": v(-2.38, -10.7) * mm, "end": v(-2.03, -10.78) * mm});
            skLineSegment(sketch, "E190", {"start": v(-2.03, -10.78) * mm, "end": v(1.66, -10.78) * mm});
            skLineSegment(sketch, "E191", {"start": v(1.66, -10.78) * mm, "end": v(2.1, -10.64) * mm});
            skLineSegment(sketch, "E192", {"start": v(2.1, -10.64) * mm, "end": v(2.4, -10.33) * mm});
            skLineSegment(sketch, "E193", {"start": v(2.4, -10.33) * mm, "end": v(2.65, -9.86) * mm});
            skLineSegment(sketch, "E194", {"start": v(2.65, -9.86) * mm, "end": v(2.74, -9.13) * mm});
            skLineSegment(sketch, "E195", {"start": v(2.74, -9.13) * mm, "end": v(2.74, -8.58) * mm});
            skLineSegment(sketch, "E196", {"start": v(2.74, -8.58) * mm, "end": v(2.7, -7.86) * mm});
            skLineSegment(sketch, "E197", {"start": v(2.7, -7.86) * mm, "end": v(2.6, -7.15) * mm});
            skLineSegment(sketch, "E198", {"start": v(2.6, -7.15) * mm, "end": v(2.38, -6.47) * mm});
            skLineSegment(sketch, "E199", {"start": v(0, -9.98) * mm, "end": v(-2.13, -9.98) * mm});
            skLineSegment(sketch, "E200", {"start": v(-2.13, -9.98) * mm, "end": v(-2.29, -9.2) * mm});
            skLineSegment(sketch, "E201", {"start": v(-2.29, -9.2) * mm, "end": v(-2.35, -8.56) * mm});
            skLineSegment(sketch, "E202", {"start": v(-2.35, -8.56) * mm, "end": v(-2.28, -7.86) * mm});
            skLineSegment(sketch, "E203", {"start": v(-2.28, -7.86) * mm, "end": v(-1.98, -7.3) * mm});
            skLineSegment(sketch, "E204", {"start": v(-1.98, -7.3) * mm, "end": v(-1.53, -7.07) * mm});
            skLineSegment(sketch, "E205", {"start": v(-1.53, -7.07) * mm, "end": v(-1.1, -7.07) * mm});
            skLineSegment(sketch, "E206", {"start": v(-1.1, -7.07) * mm, "end": v(-0.7, -7.15) * mm});
            skLineSegment(sketch, "E207", {"start": v(-0.7, -7.15) * mm, "end": v(-0.43, -7.46) * mm});
            skLineSegment(sketch, "E208", {"start": v(-0.43, -7.46) * mm, "end": v(-0.28, -7.99) * mm});
            skLineSegment(sketch, "E209", {"start": v(-2.13, -11.75) * mm, "end": v(-2.49, -11.85) * mm});
            skLineSegment(sketch, "E210", {"start": v(-2.49, -11.85) * mm, "end": v(-2.79, -12.39) * mm});
            skLineSegment(sketch, "E211", {"start": v(-2.79, -12.39) * mm, "end": v(-2.93, -13.4) * mm});
            skLineSegment(sketch, "E212", {"start": v(-2.93, -13.4) * mm, "end": v(-2.93, -14.9) * mm});
            skLineSegment(sketch, "E213", {"start": v(-2.93, -14.9) * mm, "end": v(-2.74, -15.47) * mm});
            skLineSegment(sketch, "E214", {"start": v(-2.74, -15.47) * mm, "end": v(-2.3, -15.95) * mm});
            skLineSegment(sketch, "E215", {"start": v(-2.3, -15.95) * mm, "end": v(-1.74, -16.32) * mm});
            skLineSegment(sketch, "E216", {"start": v(-1.74, -16.32) * mm, "end": v(-1, -16.46) * mm});
            skLineSegment(sketch, "E217", {"start": v(-1, -16.46) * mm, "end": v(0.89, -16.46) * mm});
            skLineSegment(sketch, "E218", {"start": v(0.89, -16.46) * mm, "end": v(1.52, -16.35) * mm});
            skLineSegment(sketch, "E219", {"start": v(1.52, -16.35) * mm, "end": v(2.08, -16.1) * mm});
            skLineSegment(sketch, "E220", {"start": v(2.08, -16.1) * mm, "end": v(2.42, -15.7) * mm});
            skLineSegment(sketch, "E221", {"start": v(2.42, -15.7) * mm, "end": v(2.67, -15.19) * mm});
            skLineSegment(sketch, "E222", {"start": v(2.67, -15.19) * mm, "end": v(2.75, -14.63) * mm});
            skLineSegment(sketch, "E223", {"start": v(2.75, -14.63) * mm, "end": v(2.75, -13.97) * mm});
            skLineSegment(sketch, "E224", {"start": v(2.75, -13.97) * mm, "end": v(2.69, -13.41) * mm});
            skLineSegment(sketch, "E225", {"start": v(2.69, -13.41) * mm, "end": v(2.55, -12.84) * mm});
            skLineSegment(sketch, "E226", {"start": v(2.55, -12.84) * mm, "end": v(2.45, -12.55) * mm});
            skLineSegment(sketch, "E227", {"start": v(1.84, -12.55) * mm, "end": v(1.94, -12.9) * mm});
            skLineSegment(sketch, "E228", {"start": v(1.94, -12.9) * mm, "end": v(2.08, -13.53) * mm});
            skLineSegment(sketch, "E229", {"start": v(2.08, -13.53) * mm, "end": v(2.13, -14.03) * mm});
            skLineSegment(sketch, "E230", {"start": v(2.13, -14.03) * mm, "end": v(2.13, -14.63) * mm});
            skLineSegment(sketch, "E231", {"start": v(2.13, -14.63) * mm, "end": v(1.98, -15.06) * mm});
            skLineSegment(sketch, "E232", {"start": v(1.98, -15.06) * mm, "end": v(1.68, -15.39) * mm});
            skLineSegment(sketch, "E233", {"start": v(1.68, -15.39) * mm, "end": v(1.2, -15.58) * mm});
            skLineSegment(sketch, "E234", {"start": v(1.2, -15.58) * mm, "end": v(0.83, -15.64) * mm});
            skLineSegment(sketch, "E235", {"start": v(0.83, -15.64) * mm, "end": v(-0.88, -15.64) * mm});
            skLineSegment(sketch, "E236", {"start": v(-0.88, -15.64) * mm, "end": v(-1.54, -15.47) * mm});
            skLineSegment(sketch, "E237", {"start": v(-1.54, -15.47) * mm, "end": v(-1.93, -15.15) * mm});
            skLineSegment(sketch, "E238", {"start": v(-1.93, -15.15) * mm, "end": v(-2.23, -14.64) * mm});
            skLineSegment(sketch, "E239", {"start": v(-2.23, -14.64) * mm, "end": v(-2.33, -13.84) * mm});
            skLineSegment(sketch, "E240", {"start": v(-2.33, -13.84) * mm, "end": v(-2.25, -13.05) * mm});
            skLineSegment(sketch, "E241", {"start": v(-2.25, -13.05) * mm, "end": v(-2.13, -12.55) * mm});
            skLineSegment(sketch, "E242.trimOffspring", {"start": v(2.45, -12.55) * mm, "end": v(5, -12.55) * mm});
            skLineSegment(sketch, "E243", {"start": v(2.5, -20.99) * mm, "end": v(1.82, -20.91) * mm});
            skLineSegment(sketch, "E244", {"start": v(1.82, -20.91) * mm, "end": v(1.94, -20.32) * mm});
            skLineSegment(sketch, "E245", {"start": v(1.94, -20.32) * mm, "end": v(2.09, -19.47) * mm});
            skLineSegment(sketch, "E246", {"start": v(2.09, -19.47) * mm, "end": v(2.09, -18.94) * mm});
            skLineSegment(sketch, "E247", {"start": v(2.09, -18.94) * mm, "end": v(1.97, -18.5) * mm});
            skLineSegment(sketch, "E248", {"start": v(1.97, -18.5) * mm, "end": v(1.7, -18.08) * mm});
            skLineSegment(sketch, "E249", {"start": v(1.7, -18.08) * mm, "end": v(1.35, -17.94) * mm});
            skLineSegment(sketch, "E250", {"start": v(1.35, -17.94) * mm, "end": v(0.91, -17.94) * mm});
            skLineSegment(sketch, "E251", {"start": v(0.91, -17.94) * mm, "end": v(0.55, -18.2) * mm});
            skLineSegment(sketch, "E252", {"start": v(0.55, -18.2) * mm, "end": v(0.37, -18.78) * mm});
            skLineSegment(sketch, "E253", {"start": v(0.37, -18.78) * mm, "end": v(0.31, -19.5) * mm});
            skLineSegment(sketch, "E254", {"start": v(0.31, -19.5) * mm, "end": v(0.17, -20.2) * mm});
            skLineSegment(sketch, "E255", {"start": v(0.17, -20.2) * mm, "end": v(-0.09, -20.75) * mm});
            skLineSegment(sketch, "E256", {"start": v(-0.09, -20.75) * mm, "end": v(-0.63, -21.12) * mm});
            skLineSegment(sketch, "E257", {"start": v(-0.63, -21.12) * mm, "end": v(-1.19, -21.2) * mm});
            skLineSegment(sketch, "E258", {"start": v(-1.19, -21.2) * mm, "end": v(-1.88, -21.15) * mm});
            skLineSegment(sketch, "E259", {"start": v(-1.88, -21.15) * mm, "end": v(-2.3, -20.92) * mm});
            skLineSegment(sketch, "E260", {"start": v(-2.3, -20.92) * mm, "end": v(-2.7, -20.43) * mm});
            skLineSegment(sketch, "E261", {"start": v(-2.7, -20.43) * mm, "end": v(-2.88, -19.93) * mm});
            skLineSegment(sketch, "E262", {"start": v(-2.88, -19.93) * mm, "end": v(-2.98, -19.03) * mm});
            skLineSegment(sketch, "E263", {"start": v(-2.98, -19.03) * mm, "end": v(-2.9, -18.13) * mm});
            skLineSegment(sketch, "E264", {"start": v(-2.9, -18.13) * mm, "end": v(-2.73, -17.42) * mm});
            skLineSegment(sketch, "E265", {"start": v(-2.73, -17.42) * mm, "end": v(-2.59, -17) * mm});
            skLineSegment(sketch, "E266", {"start": v(-2.59, -17) * mm, "end": v(-1.92, -17.24) * mm});
            skLineSegment(sketch, "E267", {"start": v(-1.92, -17.24) * mm, "end": v(-2.08, -17.7) * mm});
            skLineSegment(sketch, "E268", {"start": v(-2.08, -17.7) * mm, "end": v(-2.23, -18.34) * mm});
            skLineSegment(sketch, "E269", {"start": v(-2.23, -18.34) * mm, "end": v(-2.3, -19) * mm});
            skLineSegment(sketch, "E270", {"start": v(-2.3, -19) * mm, "end": v(-2.2, -19.72) * mm});
            skLineSegment(sketch, "E271", {"start": v(-2.2, -19.72) * mm, "end": v(-2.01, -20.12) * mm});
            skLineSegment(sketch, "E272", {"start": v(-2.01, -20.12) * mm, "end": v(-1.72, -20.32) * mm});
            skLineSegment(sketch, "E273", {"start": v(-1.72, -20.32) * mm, "end": v(-1.26, -20.38) * mm});
            skLineSegment(sketch, "E274", {"start": v(-1.26, -20.38) * mm, "end": v(-0.9, -20.32) * mm});
            skLineSegment(sketch, "E275", {"start": v(-0.9, -20.32) * mm, "end": v(-0.65, -20.09) * mm});
            skLineSegment(sketch, "E276", {"start": v(-0.65, -20.09) * mm, "end": v(-0.5, -19.66) * mm});
            skLineSegment(sketch, "E277", {"start": v(-0.5, -19.66) * mm, "end": v(-0.42, -19.15) * mm});
            skLineSegment(sketch, "E278", {"start": v(-0.42, -19.15) * mm, "end": v(-0.34, -18.48) * mm});
            skLineSegment(sketch, "E279", {"start": v(-0.34, -18.48) * mm, "end": v(-0.17, -17.94) * mm});
            skLineSegment(sketch, "E280", {"start": v(-0.17, -17.94) * mm, "end": v(0, -17.61) * mm});
            skLineSegment(sketch, "E281", {"start": v(0, -17.61) * mm, "end": v(0.37, -17.27) * mm});
            skLineSegment(sketch, "E282", {"start": v(0.37, -17.27) * mm, "end": v(0.86, -17.12) * mm});
            skLineSegment(sketch, "E283", {"start": v(0.86, -17.12) * mm, "end": v(1.45, -17.12) * mm});
            skLineSegment(sketch, "E284", {"start": v(1.45, -17.12) * mm, "end": v(1.83, -17.24) * mm});
            skLineSegment(sketch, "E285", {"start": v(1.83, -17.24) * mm, "end": v(2.16, -17.47) * mm});
            skLineSegment(sketch, "E286", {"start": v(2.16, -17.47) * mm, "end": v(2.46, -17.83) * mm});
            skLineSegment(sketch, "E287", {"start": v(2.46, -17.83) * mm, "end": v(2.66, -18.33) * mm});
            skLineSegment(sketch, "E288", {"start": v(2.66, -18.33) * mm, "end": v(2.74, -18.92) * mm});
            skLineSegment(sketch, "E289", {"start": v(2.74, -18.92) * mm, "end": v(2.74, -19.47) * mm});
            skLineSegment(sketch, "E290", {"start": v(2.74, -19.47) * mm, "end": v(2.67, -20.22) * mm});
            skLineSegment(sketch, "E291", {"start": v(2.67, -20.22) * mm, "end": v(2.5, -20.99) * mm});
            skLineSegment(sketch, "E292", {"start": v(-0.28, -7.99) * mm, "end": v(0, -9.98) * mm});
            skLineSegment(sketch, "E293", {"start": v(1.59, -28.84) * mm, "end": v(-2.65, -30.38) * mm});
            skArc(sketch, "E294", {"start": v(-2.65, -30.38) * mm, "mid": v(-2.93, -30.68) * mm, "end": v(-2.86, -31.08) * mm});
            skLineSegment(sketch, "E295", {"start": v(-2.86, -31.08) * mm, "end": v(-1.1, -33.17) * mm});
            skLineSegment(sketch, "E296", {"start": v(1.95, -29.53) * mm, "end": v(0.25, -32) * mm});
            skArc(sketch, "E297", {"start": v(-1.1, -33.17) * mm, "mid": v(-0.8, -33.3) * mm, "end": v(-0.54, -33.14) * mm});
            skLineSegment(sketch, "E298", {"start": v(2.33, -28.84) * mm, "end": v(4.83, -33) * mm});
            skLineSegment(sketch, "E299", {"start": v(4.81, -33.55) * mm, "end": v(4.3, -34.33) * mm});
            skLineSegment(sketch, "E300", {"start": v(1.95, -29.53) * mm, "end": v(3.25, -33.9) * mm});
            skLineSegment(sketch, "E301", {"start": v(3.25, -33.9) * mm, "end": v(0.25, -32) * mm});
            skLineSegment(sketch, "E302", {"start": v(-0.05, -32.44) * mm, "end": v(3.17, -34.56) * mm});
            skArc(sketch, "E303", {"start": v(3.17, -34.56) * mm, "mid": v(3.78, -34.68) * mm, "end": v(4.3, -34.33) * mm});
            skArc(sketch, "E304", {"start": v(4.81, -33.55) * mm, "mid": v(4.9, -33.28) * mm, "end": v(4.83, -33) * mm});
            skLineSegment(sketch, "E305.MirrorCS", {"start": v(1.59, -28.84) * mm, "end": v(-2.69, -27.43) * mm});
            skArc(sketch, "E306.MirrorCS", {"start": v(-2.69, -27.43) * mm, "mid": v(-2.98, -27.12) * mm, "end": v(-2.89, -26.7) * mm});
            skLineSegment(sketch, "E307.MirrorCS", {"start": v(-2.89, -26.7) * mm, "end": v(-1.08, -24.63) * mm});
            skArc(sketch, "E308.MirrorCS", {"start": v(-1.08, -24.63) * mm, "mid": v(-0.8, -24.5) * mm, "end": v(-0.52, -24.66) * mm});
            skLineSegment(sketch, "E309.MirrorCS", {"start": v(3.25, -23.91) * mm, "end": v(0.27, -25.81) * mm});
            skLineSegment(sketch, "E310.MirrorCS", {"start": v(1.98, -28.3) * mm, "end": v(3.25, -23.91) * mm});
            skLineSegment(sketch, "E311.MirrorCS", {"start": v(1.98, -28.3) * mm, "end": v(0.27, -25.81) * mm});
            skLineSegment(sketch, "E312.MirrorCS", {"start": v(-0.04, -25.37) * mm, "end": v(3.37, -23.12) * mm});
            skArc(sketch, "E313.MirrorCS", {"start": v(3.37, -23.12) * mm, "mid": v(3.88, -23.03) * mm, "end": v(4.29, -23.34) * mm});
            skLineSegment(sketch, "E314.MirrorCS", {"start": v(4.8, -24.26) * mm, "end": v(4.29, -23.34) * mm});
            skArc(sketch, "E315.MirrorCS", {"start": v(4.8, -24.26) * mm, "mid": v(4.87, -24.53) * mm, "end": v(4.8, -24.8) * mm});
            skLineSegment(sketch, "E316.MirrorCS", {"start": v(2.33, -28.84) * mm, "end": v(4.8, -24.8) * mm});
            skLineSegment(sketch, "E317", {"start": v(2.95, -26.86) * mm, "end": v(4.4, -24.57) * mm});
            skLineSegment(sketch, "E318", {"start": v(4.4, -24.57) * mm, "end": v(3.9, -23.69) * mm});
            skLineSegment(sketch, "E319", {"start": v(3.9, -23.69) * mm, "end": v(2.95, -26.86) * mm});
            skLineSegment(sketch, "E320", {"start": v(-0.5, -25.69) * mm, "end": v(-1.08, -26.1) * mm});
            skLineSegment(sketch, "E321", {"start": v(-0.16, -26.12) * mm, "end": v(-0.64, -26.42) * mm});
            skLineSegment(sketch, "E322", {"start": v(-0.64, -26.42) * mm, "end": v(0.74, -27.46) * mm});
            skLineSegment(sketch, "E323", {"start": v(0.74, -27.46) * mm, "end": v(-0.16, -26.12) * mm});
            skLineSegment(sketch, "E324", {"start": v(-0.5, -25.69) * mm, "end": v(-0.85, -25.16) * mm});
            skLineSegment(sketch, "E325", {"start": v(-0.85, -25.16) * mm, "end": v(-2.37, -26.93) * mm});
            skLineSegment(sketch, "E326", {"start": v(-2.37, -26.93) * mm, "end": v(0.56, -28) * mm});
            skLineSegment(sketch, "E327", {"start": v(0.56, -28) * mm, "end": v(-1.1, -26.8) * mm});
            skArc(sketch, "E328", {"start": v(-1.08, -26.1) * mm, "mid": v(-1.27, -26.45) * mm, "end": v(-1.1, -26.8) * mm});
            skLineSegment(sketch, "E329.trimOffspring", {"start": v(-0.05, -32.44) * mm, "end": v(-0.54, -33.14) * mm});
            skLineSegment(sketch, "E330.trimOffspring", {"start": v(-0.04, -25.37) * mm, "end": v(-0.52, -24.66) * mm});
            skFitSpline(sketch, "E331", {"points": [v(2.8, 12.8) * mm, v(2.67, 11.77) * mm, v(1.99, 10.58) * mm, v(0.65, 10.2) * mm, v(-0.86, 10.2) * mm, v(-1.75, 10.38) * mm, v(-2.52, 11.02) * mm, v(-2.92, 12) * mm, v(-2.96, 13.7) * mm, v(-2.62, 14.7) * mm, v(-1.88, 15.34) * mm, v(-0.63, 15.64) * mm, v(0.85, 15.64) * mm, v(1.7, 15.36) * mm, v(2.5, 14.57) * mm, v(2.76, 13.53) * mm, v(2.8, 12.8) * mm]});
            skSolve(sketch);
        }
        {
            var Q0;
            Q0 = qSketchRegion(id + "F18", true);
            extrude(context, id + "F19", {"entities" : qUnion([Q0]), "operationType" : NewBodyOperationType.REMOVE, "oppositeDirection" : true, "depth" : 1.8 * mm, "offsetDistance" : 25.4 * mm});
        }
    });
